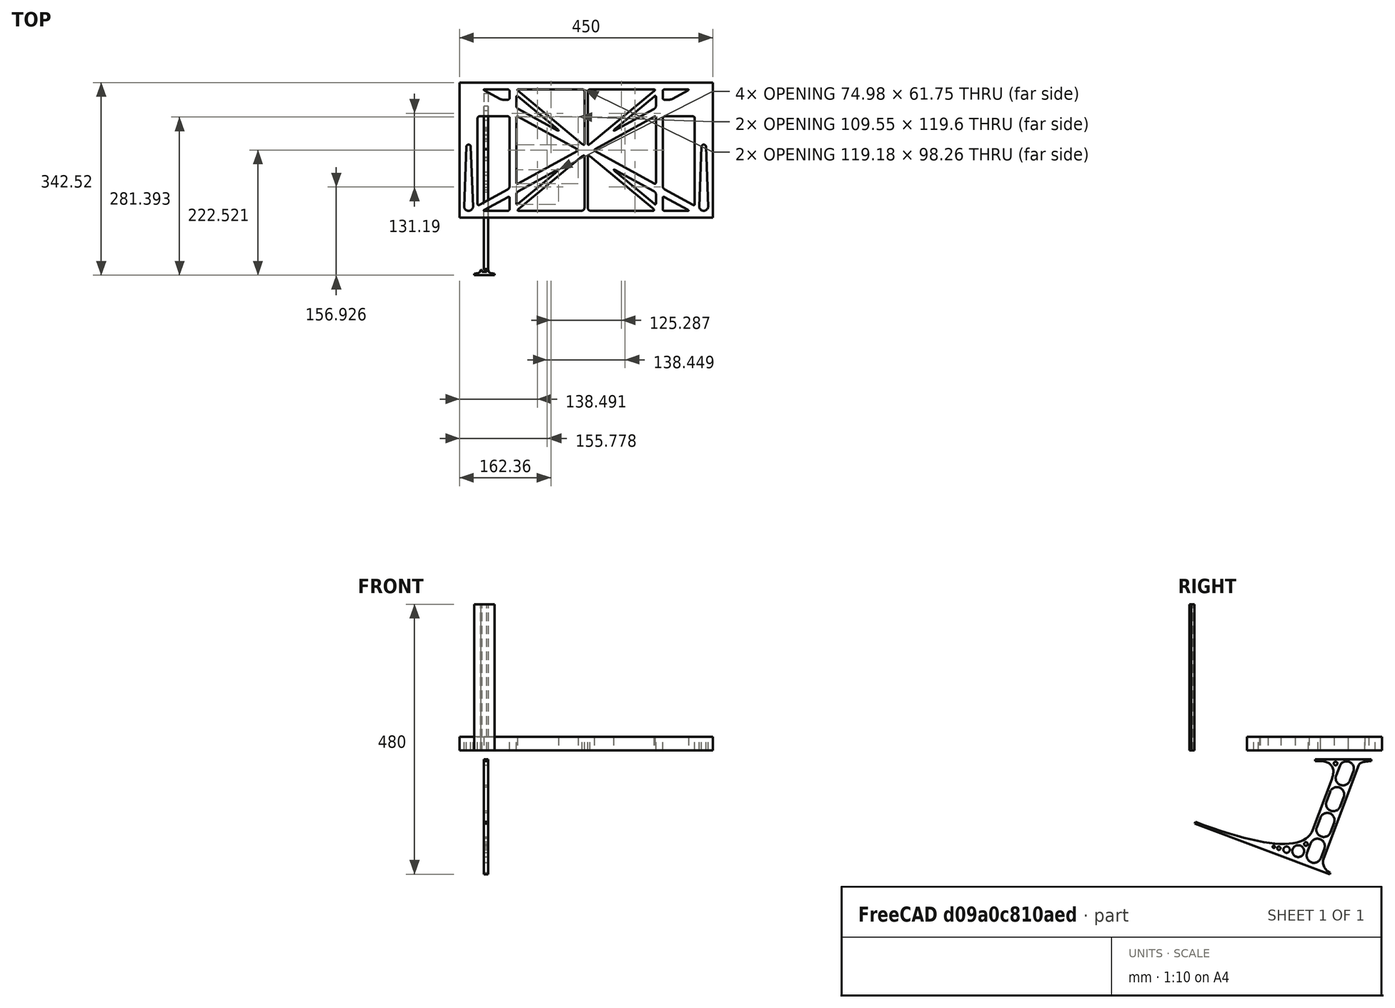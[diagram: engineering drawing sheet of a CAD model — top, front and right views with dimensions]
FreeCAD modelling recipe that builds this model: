
FCSTD DOCUMENT  (FreeCAD 0.19R0.19.2)
Label: laptopStand171FCStd
License: All rights reserved
LicenseURL: http://en.wikipedia.org/wiki/All_rights_reserved
objects: Sketcher::SketchObject×4, Part::Extrusion×3
note: 7 computed .brp shape members not serialized (recipe doc carries the construction recipe); baked Part::Feature solids carry a one-line shape summary decoded from their .brp

FEATURE [Sketcher::SketchObject] Sketch
  FullyConstrained = false
  sketch-geometry (349):
    g0: LineSegment StartX=-10.9272 StartY=-82.7794 StartZ=0 EndX=46.0728 EndY=-51.4823 EndZ=0
    g1: LineSegment StartX=-10.9272 StartY=76.4095 StartZ=0 EndX=-10.9272 EndY=-82.7794 EndZ=0
    g2: LineSegment StartX=46.0728 StartY=76.4095 StartZ=0 EndX=46.0728 EndY=-51.4823 EndZ=0
    g3: LineSegment StartX=-42.9272 StartY=136.221 StartZ=0 EndX=-42.9272 EndY=-103.779 EndZ=0
    g4: LineSegment StartX=407.073 StartY=136.221 StartZ=0 EndX=407.073 EndY=-103.779 EndZ=0
    g5: ArcOfCircle CenterX=-26.9272 CenterY=-83.7794 CenterZ=0 NormalX=0 NormalY=0 NormalZ=1 AngleXU=0 Radius=8 StartAngle=3.14159 EndAngle=6.28319
    g6: ArcOfCircle CenterX=391.073 CenterY=22.1087 CenterZ=0 NormalX=0 NormalY=0 NormalZ=1 AngleXU=0 Radius=8 StartAngle=-4.4e-15 EndAngle=3.14159
    g7: LineSegment StartX=399.073 StartY=22.1087 StartZ=0 EndX=399.073 EndY=-83.7794 EndZ=0
    g8: LineSegment StartX=383.073 StartY=22.1087 StartZ=0 EndX=383.073 EndY=-83.7794 EndZ=0
    g9: ArcOfCircle CenterX=391.073 CenterY=-83.7794 CenterZ=0 NormalX=0 NormalY=0 NormalZ=1 AngleXU=0 Radius=8 StartAngle=3.14159 EndAngle=6.28319
    g10: Circle CenterX=175.022 CenterY=27.0628 CenterZ=0 NormalX=0 NormalY=0 NormalZ=1 AngleXU=0 Radius=1
    g11: Circle CenterX=179.022 CenterY=24.8665 CenterZ=0 NormalX=0 NormalY=0 NormalZ=1 AngleXU=0 Radius=1
    g12: Circle CenterX=179.022 CenterY=27.0628 CenterZ=0 NormalX=0 NormalY=0 NormalZ=1 AngleXU=0 Radius=1
    g13: BSplineCurve PolesCount=3 KnotsCount=2 Degree=2 IsPeriodic=0
    g14: GeomPoint X=175.022 Y=27.0628 Z=0
    g15: GeomPoint X=179.022 Y=27.0628 Z=0
    g16: Circle CenterX=189.124 CenterY=27.0628 CenterZ=0 NormalX=0 NormalY=0 NormalZ=1 AngleXU=0 Radius=1
    g17: Circle CenterX=185.124 CenterY=24.8665 CenterZ=0 NormalX=0 NormalY=0 NormalZ=1 AngleXU=0 Radius=1
    g18: Circle CenterX=185.124 CenterY=27.0628 CenterZ=0 NormalX=0 NormalY=0 NormalZ=1 AngleXU=0 Radius=1
    g19: BSplineCurve PolesCount=3 KnotsCount=2 Degree=2 IsPeriodic=0
    g20: GeomPoint X=189.124 Y=27.0628 Z=0
    g21: GeomPoint X=185.124 Y=27.0628 Z=0
    g22: Circle CenterX=175.022 CenterY=5.37834 CenterZ=0 NormalX=0 NormalY=0 NormalZ=1 AngleXU=0 Radius=1
    g23: Circle CenterX=179.022 CenterY=7.57463 CenterZ=0 NormalX=0 NormalY=0 NormalZ=1 AngleXU=0 Radius=1
    g24: Circle CenterX=179.022 CenterY=5.34704 CenterZ=0 NormalX=0 NormalY=0 NormalZ=1 AngleXU=0 Radius=1
    g25: BSplineCurve PolesCount=3 KnotsCount=2 Degree=2 IsPeriodic=0
    g26: GeomPoint X=175.022 Y=5.37834 Z=0
    g27: GeomPoint X=179.022 Y=5.34704 Z=0
    g28: Circle CenterX=189.124 CenterY=5.37834 CenterZ=0 NormalX=0 NormalY=0 NormalZ=1 AngleXU=0 Radius=1
    g29: Circle CenterX=185.124 CenterY=7.57463 CenterZ=0 NormalX=0 NormalY=0 NormalZ=1 AngleXU=0 Radius=1
    g30: Circle CenterX=185.124 CenterY=5.34704 CenterZ=0 NormalX=0 NormalY=0 NormalZ=1 AngleXU=0 Radius=1
    g31: BSplineCurve PolesCount=3 KnotsCount=2 Degree=2 IsPeriodic=0
    g32: GeomPoint X=189.124 Y=5.37834 Z=0
    g33: GeomPoint X=185.124 Y=5.34704 Z=0
    g34: Circle CenterX=165.871 CenterY=18.1458 CenterZ=0 NormalX=0 NormalY=0 NormalZ=1 AngleXU=0 Radius=1
    g35: Circle CenterX=169.377 CenterY=16.2206 CenterZ=0 NormalX=0 NormalY=0 NormalZ=1 AngleXU=0 Radius=1
    g36: Circle CenterX=165.871 CenterY=14.2954 CenterZ=0 NormalX=0 NormalY=0 NormalZ=1 AngleXU=0 Radius=1
    g37: BSplineCurve PolesCount=3 KnotsCount=2 Degree=2 IsPeriodic=0
    g38: GeomPoint X=165.871 Y=18.1458 Z=0
    g39: GeomPoint X=165.871 Y=14.2954 Z=0
    g40: Circle CenterX=198.275 CenterY=18.1458 CenterZ=0 NormalX=0 NormalY=0 NormalZ=1 AngleXU=0 Radius=1
    g41: Circle CenterX=194.768 CenterY=16.2206 CenterZ=0 NormalX=0 NormalY=0 NormalZ=1 AngleXU=0 Radius=1
    g42: Circle CenterX=198.275 CenterY=14.2954 CenterZ=0 NormalX=0 NormalY=0 NormalZ=1 AngleXU=0 Radius=1
    g43: BSplineCurve PolesCount=3 KnotsCount=2 Degree=2 IsPeriodic=0
    g44: GeomPoint X=198.275 Y=18.1458 Z=0
    g45: GeomPoint X=198.275 Y=14.2954 Z=0
    g46: LineSegment StartX=407.073 StartY=-103.779 StartZ=0 EndX=-42.9272 EndY=-103.779 EndZ=0
    g47: LineSegment StartX=407.073 StartY=136.221 StartZ=0 EndX=-42.9272 EndY=136.221 EndZ=0
    g48: LineSegment StartX=46.0728 StartY=76.4095 StartZ=0 EndX=-10.9272 EndY=76.4095 EndZ=0
    g49: Circle CenterX=125.607 CenterY=54.1951 CenterZ=0 NormalX=0 NormalY=0 NormalZ=1 AngleXU=0 Radius=1
    g50: Circle CenterX=139.632 CenterY=46.4944 CenterZ=0 NormalX=0 NormalY=0 NormalZ=1 AngleXU=0 Radius=1
    g51: Circle CenterX=127.326 CenterY=56.7187 CenterZ=0 NormalX=0 NormalY=0 NormalZ=1 AngleXU=0 Radius=1
    g52: BSplineCurve PolesCount=3 KnotsCount=2 Degree=2 IsPeriodic=0
    g53: GeomPoint X=125.607 Y=54.1951 Z=0
    g54: GeomPoint X=127.326 Y=56.7187 Z=0
    g55: Circle CenterX=236.821 CenterY=56.7187 CenterZ=0 NormalX=0 NormalY=0 NormalZ=1 AngleXU=0 Radius=1
    g56: Circle CenterX=224.513 CenterY=46.4944 CenterZ=0 NormalX=0 NormalY=0 NormalZ=1 AngleXU=0 Radius=1
    g57: Circle CenterX=238.538 CenterY=54.1951 CenterZ=0 NormalX=0 NormalY=0 NormalZ=1 AngleXU=0 Radius=1
    g58: BSplineCurve PolesCount=3 KnotsCount=2 Degree=2 IsPeriodic=0
    g59: GeomPoint X=236.821 Y=56.7187 Z=0
    g60: GeomPoint X=238.538 Y=54.1951 Z=0
    g61: Circle CenterX=238.538 CenterY=-21.7539 CenterZ=0 NormalX=0 NormalY=0 NormalZ=1 AngleXU=0 Radius=1
    g62: Circle CenterX=224.513 CenterY=-14.0532 CenterZ=0 NormalX=0 NormalY=0 NormalZ=1 AngleXU=0 Radius=1
    g63: Circle CenterX=236.821 CenterY=-24.2775 CenterZ=0 NormalX=0 NormalY=0 NormalZ=1 AngleXU=0 Radius=1
    g64: BSplineCurve PolesCount=3 KnotsCount=2 Degree=2 IsPeriodic=0
    g65: GeomPoint X=238.538 Y=-21.7539 Z=0
    g66: GeomPoint X=236.821 Y=-24.2775 Z=0
    g67: Circle CenterX=125.607 CenterY=-21.7539 CenterZ=0 NormalX=0 NormalY=0 NormalZ=1 AngleXU=0 Radius=1
    g68: Circle CenterX=139.632 CenterY=-14.0532 CenterZ=0 NormalX=0 NormalY=0 NormalZ=1 AngleXU=0 Radius=1
    g69: Circle CenterX=127.325 CenterY=-24.2775 CenterZ=0 NormalX=0 NormalY=0 NormalZ=1 AngleXU=0 Radius=1
    g70: BSplineCurve PolesCount=3 KnotsCount=2 Degree=2 IsPeriodic=0
    g71: GeomPoint X=125.607 Y=-21.7539 Z=0
    g72: GeomPoint X=127.325 Y=-24.2775 Z=0
    g73: Circle CenterX=302.996 CenterY=111.695 CenterZ=0 NormalX=0 NormalY=0 NormalZ=1 AngleXU=0 Radius=1
    g74: Circle CenterX=306.073 CenterY=114.251 CenterZ=0 NormalX=0 NormalY=0 NormalZ=1 AngleXU=0 Radius=1
    g75: Circle CenterX=306.073 CenterY=110.251 CenterZ=0 NormalX=0 NormalY=0 NormalZ=1 AngleXU=0 Radius=1
    g76: BSplineCurve PolesCount=3 KnotsCount=2 Degree=2 IsPeriodic=0
    g77: GeomPoint X=302.996 Y=111.695 Z=0
    g78: GeomPoint X=306.073 Y=110.251 Z=0
    g79: Circle CenterX=306.073 CenterY=95.2763 CenterZ=0 NormalX=0 NormalY=0 NormalZ=1 AngleXU=0 Radius=1
    g80: Circle CenterX=306.073 CenterY=91.2763 CenterZ=0 NormalX=0 NormalY=0 NormalZ=1 AngleXU=0 Radius=1
    g81: Circle CenterX=302.567 CenterY=89.3511 CenterZ=0 NormalX=0 NormalY=0 NormalZ=1 AngleXU=0 Radius=1
    g82: BSplineCurve PolesCount=3 KnotsCount=2 Degree=2 IsPeriodic=0
    g83: GeomPoint X=306.073 Y=95.2763 Z=0
    g84: GeomPoint X=302.567 Y=89.3511 Z=0
    g85: LineSegment StartX=306.073 StartY=110.251 StartZ=0 EndX=306.073 EndY=95.2763 EndZ=0
    g86: LineSegment StartX=302.996 StartY=111.695 StartZ=0 EndX=236.821 EndY=56.7187 EndZ=0
    g87: LineSegment StartX=238.538 StartY=54.1951 StartZ=0 EndX=302.567 EndY=89.3511 EndZ=0
    g88: Circle CenterX=61.1496 CenterY=111.695 CenterZ=0 NormalX=0 NormalY=0 NormalZ=1 AngleXU=0 Radius=1
    g89: Circle CenterX=58.0728 CenterY=114.251 CenterZ=0 NormalX=0 NormalY=0 NormalZ=1 AngleXU=0 Radius=1
    g90: Circle CenterX=58.0728 CenterY=110.251 CenterZ=0 NormalX=0 NormalY=0 NormalZ=1 AngleXU=0 Radius=1
    g91: BSplineCurve PolesCount=3 KnotsCount=2 Degree=2 IsPeriodic=0
    g92: GeomPoint X=61.1496 Y=111.695 Z=0
    g93: GeomPoint X=58.0728 Y=110.251 Z=0
    g94: Circle CenterX=61.5791 CenterY=89.3511 CenterZ=0 NormalX=0 NormalY=0 NormalZ=1 AngleXU=0 Radius=1
    g95: Circle CenterX=58.0728 CenterY=91.2763 CenterZ=0 NormalX=0 NormalY=0 NormalZ=1 AngleXU=0 Radius=1
    g96: Circle CenterX=58.0728 CenterY=95.2763 CenterZ=0 NormalX=0 NormalY=0 NormalZ=1 AngleXU=0 Radius=1
    g97: BSplineCurve PolesCount=3 KnotsCount=2 Degree=2 IsPeriodic=0
    g98: GeomPoint X=61.5791 Y=89.3511 Z=0
    g99: GeomPoint X=58.0728 Y=95.2763 Z=0
    g100: LineSegment StartX=58.0728 StartY=110.251 StartZ=0 EndX=58.0728 EndY=95.2763 EndZ=0
    g101: LineSegment StartX=61.1496 StartY=111.695 StartZ=0 EndX=127.326 EndY=56.7187 EndZ=0
    g102: LineSegment StartX=125.607 StartY=54.1951 StartZ=0 EndX=61.5791 EndY=89.3511 EndZ=0
    g103: Circle CenterX=61.5791 CenterY=-56.9099 CenterZ=0 NormalX=0 NormalY=0 NormalZ=1 AngleXU=0 Radius=1
    g104: Circle CenterX=58.0728 CenterY=-58.8351 CenterZ=0 NormalX=0 NormalY=0 NormalZ=1 AngleXU=0 Radius=1
    g105: Circle CenterX=58.0728 CenterY=-62.8351 CenterZ=0 NormalX=0 NormalY=0 NormalZ=1 AngleXU=0 Radius=1
    g106: BSplineCurve PolesCount=3 KnotsCount=2 Degree=2 IsPeriodic=0
    g107: GeomPoint X=61.5791 Y=-56.9099 Z=0
    g108: GeomPoint X=58.0728 Y=-62.8351 Z=0
    g109: Circle CenterX=58.0728 CenterY=-77.8102 CenterZ=0 NormalX=0 NormalY=0 NormalZ=1 AngleXU=0 Radius=1
    g110: Circle CenterX=58.0728 CenterY=-81.8102 CenterZ=0 NormalX=0 NormalY=0 NormalZ=1 AngleXU=0 Radius=1
    g111: Circle CenterX=61.1496 CenterY=-79.2541 CenterZ=0 NormalX=0 NormalY=0 NormalZ=1 AngleXU=0 Radius=1
    g112: BSplineCurve PolesCount=3 KnotsCount=2 Degree=2 IsPeriodic=0
    g113: GeomPoint X=58.0728 Y=-77.8102 Z=0
    g114: GeomPoint X=61.1496 Y=-79.2541 Z=0
    g115: LineSegment StartX=58.0728 StartY=-62.8351 StartZ=0 EndX=58.0728 EndY=-77.8102 EndZ=0
    g116: LineSegment StartX=61.1496 StartY=-79.2541 StartZ=0 EndX=127.325 EndY=-24.2775 EndZ=0
    g117: LineSegment StartX=125.607 StartY=-21.7539 StartZ=0 EndX=61.5791 EndY=-56.9099 EndZ=0
    g118: Circle CenterX=302.567 CenterY=-56.9099 CenterZ=0 NormalX=0 NormalY=0 NormalZ=1 AngleXU=0 Radius=1
    g119: Circle CenterX=306.073 CenterY=-58.8351 CenterZ=0 NormalX=0 NormalY=0 NormalZ=1 AngleXU=0 Radius=1
    g120: Circle CenterX=306.073 CenterY=-62.8351 CenterZ=0 NormalX=0 NormalY=0 NormalZ=1 AngleXU=0 Radius=1
    g121: BSplineCurve PolesCount=3 KnotsCount=2 Degree=2 IsPeriodic=0
    g122: GeomPoint X=302.567 Y=-56.9099 Z=0
    g123: GeomPoint X=306.073 Y=-62.8351 Z=0
    g124: Circle CenterX=302.996 CenterY=-79.2541 CenterZ=0 NormalX=0 NormalY=0 NormalZ=1 AngleXU=0 Radius=1
    g125: Circle CenterX=306.073 CenterY=-81.8102 CenterZ=0 NormalX=0 NormalY=0 NormalZ=1 AngleXU=0 Radius=1
    g126: Circle CenterX=306.073 CenterY=-77.8102 CenterZ=0 NormalX=0 NormalY=0 NormalZ=1 AngleXU=0 Radius=1
    g127: BSplineCurve PolesCount=3 KnotsCount=2 Degree=2 IsPeriodic=0
    g128: GeomPoint X=302.996 Y=-79.2541 Z=0
    g129: GeomPoint X=306.073 Y=-77.8102 Z=0
    g130: LineSegment StartX=306.073 StartY=-62.8351 StartZ=0 EndX=306.073 EndY=-77.8102 EndZ=0
    g131: LineSegment StartX=302.996 StartY=-79.2541 StartZ=0 EndX=236.821 EndY=-24.2775 EndZ=0
    g132: LineSegment StartX=238.538 StartY=-21.7539 StartZ=0 EndX=302.567 EndY=-56.9099 EndZ=0
    g133: Circle CenterX=61.6457 CenterY=-88.8112 CenterZ=0 NormalX=0 NormalY=0 NormalZ=1 AngleXU=0 Radius=1
    g134: Circle CenterX=58.0728 CenterY=-91.7794 CenterZ=0 NormalX=0 NormalY=0 NormalZ=1 AngleXU=0 Radius=1
    g135: Circle CenterX=63.9135 CenterY=-91.7794 CenterZ=0 NormalX=0 NormalY=0 NormalZ=1 AngleXU=0 Radius=1
    g136: BSplineCurve PolesCount=3 KnotsCount=2 Degree=2 IsPeriodic=0
    g137: GeomPoint X=61.6457 Y=-88.8112 Z=0
    g138: GeomPoint X=63.9135 Y=-91.7794 Z=0
    g139: Circle CenterX=179.022 CenterY=-85.8163 CenterZ=0 NormalX=0 NormalY=0 NormalZ=1 AngleXU=0 Radius=1
    g140: Circle CenterX=179.022 CenterY=-91.7794 CenterZ=0 NormalX=0 NormalY=0 NormalZ=1 AngleXU=0 Radius=1
    g141: Circle CenterX=171.895 CenterY=-91.7794 CenterZ=0 NormalX=0 NormalY=0 NormalZ=1 AngleXU=0 Radius=1
    g142: BSplineCurve PolesCount=3 KnotsCount=2 Degree=2 IsPeriodic=0
    g143: GeomPoint X=179.022 Y=-85.8163 Z=0
    g144: GeomPoint X=171.895 Y=-91.7794 Z=0
    g145: Circle CenterX=185.124 CenterY=-86.2028 CenterZ=0 NormalX=0 NormalY=0 NormalZ=1 AngleXU=0 Radius=1
    g146: Circle CenterX=185.124 CenterY=-91.7794 CenterZ=0 NormalX=0 NormalY=0 NormalZ=1 AngleXU=0 Radius=1
    g147: Circle CenterX=191.747 CenterY=-91.7794 CenterZ=0 NormalX=0 NormalY=0 NormalZ=1 AngleXU=0 Radius=1
    g148: BSplineCurve PolesCount=3 KnotsCount=2 Degree=2 IsPeriodic=0
    g149: GeomPoint X=185.124 Y=-86.2028 Z=0
    g150: GeomPoint X=191.747 Y=-91.7794 Z=0
    g151: Circle CenterX=299.888 CenterY=-86.6413 CenterZ=0 NormalX=0 NormalY=0 NormalZ=1 AngleXU=0 Radius=1
    g152: Circle CenterX=306.073 CenterY=-91.7794 CenterZ=0 NormalX=0 NormalY=0 NormalZ=1 AngleXU=0 Radius=1
    g153: Circle CenterX=298.776 CenterY=-91.7794 CenterZ=0 NormalX=0 NormalY=0 NormalZ=1 AngleXU=0 Radius=1
    g154: BSplineCurve PolesCount=3 KnotsCount=2 Degree=2 IsPeriodic=0
    g155: GeomPoint X=299.888 Y=-86.6413 Z=0
    g156: GeomPoint X=298.776 Y=-91.7794 Z=0
    g157: LineSegment StartX=189.124 StartY=5.37834 StartZ=0 EndX=299.888 EndY=-86.6413 EndZ=0
    g158: LineSegment StartX=298.776 StartY=-91.7794 StartZ=0 EndX=191.747 EndY=-91.7794 EndZ=0
    g159: LineSegment StartX=185.124 StartY=-86.2028 StartZ=0 EndX=185.124 EndY=5.34704 EndZ=0
    g160: LineSegment StartX=179.022 StartY=5.34704 StartZ=0 EndX=179.022 EndY=-85.8163 EndZ=0
    g161: LineSegment StartX=171.895 StartY=-91.7794 StartZ=0 EndX=63.9135 EndY=-91.7794 EndZ=0
    g162: LineSegment StartX=61.6457 StartY=-88.8112 StartZ=0 EndX=175.022 EndY=5.37834 EndZ=0
    g163: Circle CenterX=302.073 CenterY=124.221 CenterZ=0 NormalX=0 NormalY=0 NormalZ=1 AngleXU=0 Radius=1
    g164: Circle CenterX=306.073 CenterY=124.221 CenterZ=0 NormalX=0 NormalY=0 NormalZ=1 AngleXU=0 Radius=1
    g165: Circle CenterX=302.996 CenterY=121.665 CenterZ=0 NormalX=0 NormalY=0 NormalZ=1 AngleXU=0 Radius=1
    g166: BSplineCurve PolesCount=3 KnotsCount=2 Degree=2 IsPeriodic=0
    g167: GeomPoint X=302.073 Y=124.221 Z=0
    g168: GeomPoint X=302.996 Y=121.665 Z=0
    g169: Circle CenterX=189.124 CenterY=124.221 CenterZ=0 NormalX=0 NormalY=0 NormalZ=1 AngleXU=0 Radius=1
    g170: Circle CenterX=185.124 CenterY=124.221 CenterZ=0 NormalX=0 NormalY=0 NormalZ=1 AngleXU=0 Radius=1
    g171: Circle CenterX=185.124 CenterY=120.221 CenterZ=0 NormalX=0 NormalY=0 NormalZ=1 AngleXU=0 Radius=1
    g172: BSplineCurve PolesCount=3 KnotsCount=2 Degree=2 IsPeriodic=0
    g173: GeomPoint X=189.124 Y=124.221 Z=0
    g174: GeomPoint X=185.124 Y=120.221 Z=0
    g175: Circle CenterX=175.022 CenterY=124.221 CenterZ=0 NormalX=0 NormalY=0 NormalZ=1 AngleXU=0 Radius=1
    g176: Circle CenterX=179.022 CenterY=124.221 CenterZ=0 NormalX=0 NormalY=0 NormalZ=1 AngleXU=0 Radius=1
    g177: Circle CenterX=179.022 CenterY=120.221 CenterZ=0 NormalX=0 NormalY=0 NormalZ=1 AngleXU=0 Radius=1
    g178: BSplineCurve PolesCount=3 KnotsCount=2 Degree=2 IsPeriodic=0
    g179: GeomPoint X=175.022 Y=124.221 Z=0
    g180: GeomPoint X=179.022 Y=120.221 Z=0
    g181: Circle CenterX=62.0728 CenterY=124.221 CenterZ=0 NormalX=0 NormalY=0 NormalZ=1 AngleXU=0 Radius=1
    g182: Circle CenterX=58.0728 CenterY=124.221 CenterZ=0 NormalX=0 NormalY=0 NormalZ=1 AngleXU=0 Radius=1
    g183: Circle CenterX=61.1496 CenterY=121.665 CenterZ=0 NormalX=0 NormalY=0 NormalZ=1 AngleXU=0 Radius=1
    g184: BSplineCurve PolesCount=3 KnotsCount=2 Degree=2 IsPeriodic=0
    g185: GeomPoint X=62.0728 Y=124.221 Z=0
    g186: GeomPoint X=61.1496 Y=121.665 Z=0
    g187: LineSegment StartX=62.0728 StartY=124.221 StartZ=0 EndX=175.022 EndY=124.221 EndZ=0
    g188: LineSegment StartX=179.022 StartY=120.221 StartZ=0 EndX=179.022 EndY=27.0628 EndZ=0
    g189: LineSegment StartX=185.124 StartY=27.0628 StartZ=0 EndX=185.124 EndY=120.221 EndZ=0
    g190: LineSegment StartX=189.124 StartY=124.221 StartZ=0 EndX=302.073 EndY=124.221 EndZ=0
    g191: LineSegment StartX=302.996 StartY=121.665 StartZ=0 EndX=189.124 EndY=27.0628 EndZ=0
    g192: LineSegment StartX=175.022 StartY=27.0628 StartZ=0 EndX=61.1496 EndY=121.665 EndZ=0
    g193: Circle CenterX=61.5791 CenterY=75.4095 CenterZ=0 NormalX=0 NormalY=0 NormalZ=1 AngleXU=0 Radius=1
    g194: Circle CenterX=58.0728 CenterY=77.3346 CenterZ=0 NormalX=0 NormalY=0 NormalZ=1 AngleXU=0 Radius=1
    g195: Circle CenterX=58.0728 CenterY=73.3346 CenterZ=0 NormalX=0 NormalY=0 NormalZ=1 AngleXU=0 Radius=1
    g196: BSplineCurve PolesCount=3 KnotsCount=2 Degree=2 IsPeriodic=0
    g197: GeomPoint X=61.5791 Y=75.4095 Z=0
    g198: GeomPoint X=58.0728 Y=73.3346 Z=0
    g199: Circle CenterX=58.0728 CenterY=-40.8935 CenterZ=0 NormalX=0 NormalY=0 NormalZ=1 AngleXU=0 Radius=1
    g200: Circle CenterX=58.0728 CenterY=-44.8935 CenterZ=0 NormalX=0 NormalY=0 NormalZ=1 AngleXU=0 Radius=1
    g201: Circle CenterX=61.5791 CenterY=-42.9683 CenterZ=0 NormalX=0 NormalY=0 NormalZ=1 AngleXU=0 Radius=1
    g202: BSplineCurve PolesCount=3 KnotsCount=2 Degree=2 IsPeriodic=0
    g203: GeomPoint X=58.0728 Y=-40.8935 Z=0
    g204: GeomPoint X=61.5791 Y=-42.9683 Z=0
    g205: LineSegment StartX=61.5791 StartY=-42.9683 StartZ=0 EndX=165.871 EndY=14.2954 EndZ=0
    g206: LineSegment StartX=165.871 StartY=18.1458 StartZ=0 EndX=61.5791 EndY=75.4095 EndZ=0
    g207: LineSegment StartX=58.0728 StartY=73.3346 StartZ=0 EndX=58.0728 EndY=-40.8935 EndZ=0
    g208: Circle CenterX=302.567 CenterY=-42.9683 CenterZ=0 NormalX=0 NormalY=0 NormalZ=1 AngleXU=0 Radius=1
    g209: Circle CenterX=306.073 CenterY=-44.8935 CenterZ=0 NormalX=0 NormalY=0 NormalZ=1 AngleXU=0 Radius=1
    g210: Circle CenterX=306.073 CenterY=-40.8935 CenterZ=0 NormalX=0 NormalY=0 NormalZ=1 AngleXU=0 Radius=1
    g211: BSplineCurve PolesCount=3 KnotsCount=2 Degree=2 IsPeriodic=0
    g212: GeomPoint X=302.567 Y=-42.9683 Z=0
    g213: GeomPoint X=306.073 Y=-40.8935 Z=0
    g214: Circle CenterX=306.073 CenterY=73.3346 CenterZ=0 NormalX=0 NormalY=0 NormalZ=1 AngleXU=0 Radius=1
    g215: Circle CenterX=306.073 CenterY=77.3346 CenterZ=0 NormalX=0 NormalY=0 NormalZ=1 AngleXU=0 Radius=1
    g216: Circle CenterX=302.567 CenterY=75.4095 CenterZ=0 NormalX=0 NormalY=0 NormalZ=1 AngleXU=0 Radius=1
    g217: BSplineCurve PolesCount=3 KnotsCount=2 Degree=2 IsPeriodic=0
    g218: GeomPoint X=306.073 Y=73.3346 Z=0
    g219: GeomPoint X=302.567 Y=75.4095 Z=0
    g220: LineSegment StartX=302.567 StartY=-42.9683 StartZ=0 EndX=198.275 EndY=14.2954 EndZ=0
    g221: LineSegment StartX=198.275 StartY=18.1458 StartZ=0 EndX=302.567 EndY=75.4095 EndZ=0
    g222: LineSegment StartX=306.073 StartY=73.3346 StartZ=0 EndX=306.073 EndY=-40.8935 EndZ=0
    g223: LineSegment StartX=322.073 StartY=105.865 StartZ=0 EndX=328.643 EndY=105.865 EndZ=0
    g224: LineSegment StartX=318.073 StartY=120.221 StartZ=0 EndX=318.073 EndY=109.865 EndZ=0
    g225: LineSegment StartX=336.157 StartY=107.779 StartZ=0 EndX=362.567 EndY=122.294 EndZ=0
    g226: Circle CenterX=362.073 CenterY=124.221 CenterZ=0 NormalX=0 NormalY=0 NormalZ=1 AngleXU=0 Radius=1
    g227: Circle CenterX=366.073 CenterY=124.221 CenterZ=0 NormalX=0 NormalY=0 NormalZ=1 AngleXU=0 Radius=1
    g228: Circle CenterX=362.567 CenterY=122.294 CenterZ=0 NormalX=0 NormalY=0 NormalZ=1 AngleXU=0 Radius=1
    g229: BSplineCurve PolesCount=3 KnotsCount=2 Degree=2 IsPeriodic=0
    g230: GeomPoint X=362.073 Y=124.221 Z=0
    g231: GeomPoint X=362.567 Y=122.294 Z=0
    g232: Circle CenterX=322.073 CenterY=124.221 CenterZ=0 NormalX=0 NormalY=0 NormalZ=1 AngleXU=0 Radius=1
    g233: Circle CenterX=318.073 CenterY=124.221 CenterZ=0 NormalX=0 NormalY=0 NormalZ=1 AngleXU=0 Radius=1
    g234: Circle CenterX=318.073 CenterY=120.221 CenterZ=0 NormalX=0 NormalY=0 NormalZ=1 AngleXU=0 Radius=1
    g235: BSplineCurve PolesCount=3 KnotsCount=2 Degree=2 IsPeriodic=0
    g236: GeomPoint X=322.073 Y=124.221 Z=0
    g237: GeomPoint X=318.073 Y=120.221 Z=0
    g238: Circle CenterX=322.073 CenterY=105.865 CenterZ=0 NormalX=0 NormalY=0 NormalZ=1 AngleXU=0 Radius=1
    g239: Circle CenterX=318.073 CenterY=105.865 CenterZ=0 NormalX=0 NormalY=0 NormalZ=1 AngleXU=0 Radius=1
    g240: Circle CenterX=318.073 CenterY=109.865 CenterZ=0 NormalX=0 NormalY=0 NormalZ=1 AngleXU=0 Radius=1
    g241: BSplineCurve PolesCount=3 KnotsCount=2 Degree=2 IsPeriodic=0
    g242: GeomPoint X=322.073 Y=105.865 Z=0
    g243: GeomPoint X=318.073 Y=109.865 Z=0
    g244: Circle CenterX=336.157 CenterY=107.779 CenterZ=0 NormalX=0 NormalY=0 NormalZ=1 AngleXU=0 Radius=1
    g245: Circle CenterX=332.651 CenterY=105.853 CenterZ=0 NormalX=0 NormalY=0 NormalZ=1 AngleXU=0 Radius=1
    g246: Circle CenterX=328.643 CenterY=105.865 CenterZ=0 NormalX=0 NormalY=0 NormalZ=1 AngleXU=0 Radius=1
    g247: BSplineCurve PolesCount=3 KnotsCount=2 Degree=2 IsPeriodic=0
    g248: GeomPoint X=336.157 Y=107.779 Z=0
    g249: GeomPoint X=328.643 Y=105.865 Z=0
    g250: LineSegment StartX=322.073 StartY=124.221 StartZ=0 EndX=362.073 EndY=124.221 EndZ=0
    g251: Circle CenterX=371.567 CenterY=-80.8644 CenterZ=0 NormalX=0 NormalY=0 NormalZ=1 AngleXU=0 Radius=1
    g252: Circle CenterX=375.073 CenterY=-82.7896 CenterZ=0 NormalX=0 NormalY=0 NormalZ=1 AngleXU=0 Radius=1
    g253: Circle CenterX=375.073 CenterY=-78.7896 CenterZ=0 NormalX=0 NormalY=0 NormalZ=1 AngleXU=0 Radius=1
    g254: BSplineCurve PolesCount=3 KnotsCount=2 Degree=2 IsPeriodic=0
    g255: GeomPoint X=371.567 Y=-80.8644 Z=0
    g256: GeomPoint X=375.073 Y=-78.7896 Z=0
    g257: Circle CenterX=321.579 CenterY=-53.4075 CenterZ=0 NormalX=0 NormalY=0 NormalZ=1 AngleXU=0 Radius=1
    g258: Circle CenterX=318.073 CenterY=-51.4823 CenterZ=0 NormalX=0 NormalY=0 NormalZ=1 AngleXU=0 Radius=1
    g259: Circle CenterX=318.073 CenterY=-47.4805 CenterZ=0 NormalX=0 NormalY=0 NormalZ=1 AngleXU=0 Radius=1
    g260: BSplineCurve PolesCount=3 KnotsCount=2 Degree=2 IsPeriodic=0
    g261: GeomPoint X=321.579 Y=-53.4075 Z=0
    g262: GeomPoint X=318.073 Y=-47.4805 Z=0
    g263: LineSegment StartX=371.567 StartY=-80.8644 StartZ=0 EndX=321.579 EndY=-53.4075 EndZ=0
    g264: Circle CenterX=321.579 CenterY=-67.3492 CenterZ=0 NormalX=0 NormalY=0 NormalZ=1 AngleXU=0 Radius=1
    g265: Circle CenterX=318.073 CenterY=-65.424 CenterZ=0 NormalX=0 NormalY=0 NormalZ=1 AngleXU=0 Radius=1
    g266: Circle CenterX=318.073 CenterY=-69.424 CenterZ=0 NormalX=0 NormalY=0 NormalZ=1 AngleXU=0 Radius=1
    g267: BSplineCurve PolesCount=3 KnotsCount=2 Degree=2 IsPeriodic=0
    g268: GeomPoint X=321.579 Y=-67.3492 Z=0
    g269: GeomPoint X=318.073 Y=-69.424 Z=0
    g270: Circle CenterX=362.567 CenterY=-89.8542 CenterZ=0 NormalX=0 NormalY=0 NormalZ=1 AngleXU=0 Radius=1
    g271: Circle CenterX=366.073 CenterY=-91.7794 CenterZ=0 NormalX=0 NormalY=0 NormalZ=1 AngleXU=0 Radius=1
    g272: Circle CenterX=362.073 CenterY=-91.7794 CenterZ=0 NormalX=0 NormalY=0 NormalZ=1 AngleXU=0 Radius=1
    g273: BSplineCurve PolesCount=3 KnotsCount=2 Degree=2 IsPeriodic=0
    g274: GeomPoint X=362.567 Y=-89.8542 Z=0
    g275: GeomPoint X=362.073 Y=-91.7794 Z=0
    g276: Circle CenterX=322.073 CenterY=-91.7794 CenterZ=0 NormalX=0 NormalY=0 NormalZ=1 AngleXU=0 Radius=1
    g277: Circle CenterX=318.073 CenterY=-91.7794 CenterZ=0 NormalX=0 NormalY=0 NormalZ=1 AngleXU=0 Radius=1
    g278: Circle CenterX=318.073 CenterY=-87.7794 CenterZ=0 NormalX=0 NormalY=0 NormalZ=1 AngleXU=0 Radius=1
    g279: BSplineCurve PolesCount=3 KnotsCount=2 Degree=2 IsPeriodic=0
    g280: GeomPoint X=322.073 Y=-91.7794 Z=0
    g281: GeomPoint X=318.073 Y=-87.7794 Z=0
    g282: LineSegment StartX=362.567 StartY=-89.8542 StartZ=0 EndX=321.579 EndY=-67.3492 EndZ=0
    g283: LineSegment StartX=318.073 StartY=-69.424 StartZ=0 EndX=318.073 EndY=-87.7794 EndZ=0
    g284: LineSegment StartX=322.073 StartY=-91.7794 StartZ=0 EndX=362.073 EndY=-91.7794 EndZ=0
    g285: Circle CenterX=2.07281 CenterY=124.221 CenterZ=0 NormalX=0 NormalY=0 NormalZ=1 AngleXU=0 Radius=1
    g286: Circle CenterX=1.57905 CenterY=122.295 CenterZ=0 NormalX=0 NormalY=0 NormalZ=1 AngleXU=0 Radius=1
    g287: BSplineCurve PolesCount=3 KnotsCount=2 Degree=2 IsPeriodic=0
    g288: GeomPoint X=2.07281 Y=124.221 Z=0
    g289: GeomPoint X=1.57905 Y=122.295 Z=0
    g290: Circle CenterX=42.0728 CenterY=124.221 CenterZ=0 NormalX=0 NormalY=0 NormalZ=1 AngleXU=0 Radius=1
    g291: Circle CenterX=46.0728 CenterY=124.221 CenterZ=0 NormalX=0 NormalY=0 NormalZ=1 AngleXU=0 Radius=1
    g292: Circle CenterX=46.0728 CenterY=120.221 CenterZ=0 NormalX=0 NormalY=0 NormalZ=1 AngleXU=0 Radius=1
    g293: BSplineCurve PolesCount=3 KnotsCount=2 Degree=2 IsPeriodic=0
    g294: GeomPoint X=42.0728 Y=124.221 Z=0
    g295: GeomPoint X=46.0728 Y=120.221 Z=0
    g296: Circle CenterX=46.0728 CenterY=109.865 CenterZ=0 NormalX=0 NormalY=0 NormalZ=1 AngleXU=0 Radius=1
    g297: Circle CenterX=46.0728 CenterY=105.865 CenterZ=0 NormalX=0 NormalY=0 NormalZ=1 AngleXU=0 Radius=1
    g298: Circle CenterX=42.0728 CenterY=105.865 CenterZ=0 NormalX=0 NormalY=0 NormalZ=1 AngleXU=0 Radius=1
    g299: BSplineCurve PolesCount=3 KnotsCount=2 Degree=2 IsPeriodic=0
    g300: GeomPoint X=46.0728 Y=109.865 Z=0
    g301: GeomPoint X=42.0728 Y=105.865 Z=0
    g302: Circle CenterX=35.5028 CenterY=105.865 CenterZ=0 NormalX=0 NormalY=0 NormalZ=1 AngleXU=0 Radius=1
    g303: Circle CenterX=31.5028 CenterY=105.865 CenterZ=0 NormalX=0 NormalY=0 NormalZ=1 AngleXU=0 Radius=1
    g304: Circle CenterX=27.9965 CenterY=107.79 CenterZ=0 NormalX=0 NormalY=0 NormalZ=1 AngleXU=0 Radius=1
    g305: BSplineCurve PolesCount=3 KnotsCount=2 Degree=2 IsPeriodic=0
    g306: GeomPoint X=35.5028 Y=105.865 Z=0
    g307: GeomPoint X=27.9965 Y=107.79 Z=0
    g308: LineSegment StartX=2.07281 StartY=124.221 StartZ=0 EndX=42.0728 EndY=124.221 EndZ=0
    g309: LineSegment StartX=46.0728 StartY=120.221 StartZ=0 EndX=46.0728 EndY=109.865 EndZ=0
    g310: LineSegment StartX=42.0728 StartY=105.865 StartZ=0 EndX=35.5028 EndY=105.865 EndZ=0
    g311: LineSegment StartX=27.9965 StartY=107.79 StartZ=0 EndX=1.57905 EndY=122.295 EndZ=0
    g312: Circle CenterX=42.5666 CenterY=-67.3492 CenterZ=0 NormalX=0 NormalY=0 NormalZ=1 AngleXU=0 Radius=1
    g313: Circle CenterX=46.0728 CenterY=-65.424 CenterZ=0 NormalX=0 NormalY=0 NormalZ=1 AngleXU=0 Radius=1
    g314: Circle CenterX=46.0728 CenterY=-69.424 CenterZ=0 NormalX=0 NormalY=0 NormalZ=1 AngleXU=0 Radius=1
    g315: BSplineCurve PolesCount=3 KnotsCount=2 Degree=2 IsPeriodic=0
    g316: GeomPoint X=42.5666 Y=-67.3492 Z=0
    g317: GeomPoint X=46.0728 Y=-69.424 Z=0
    g318: Circle CenterX=46.0728 CenterY=-87.7794 CenterZ=0 NormalX=0 NormalY=0 NormalZ=1 AngleXU=0 Radius=1
    g319: Circle CenterX=46.0728 CenterY=-91.7794 CenterZ=0 NormalX=0 NormalY=0 NormalZ=1 AngleXU=0 Radius=1
    g320: Circle CenterX=42.0728 CenterY=-91.7794 CenterZ=0 NormalX=0 NormalY=0 NormalZ=1 AngleXU=0 Radius=1
    g321: BSplineCurve PolesCount=3 KnotsCount=2 Degree=2 IsPeriodic=0
    g322: GeomPoint X=46.0728 Y=-87.7794 Z=0
    g323: GeomPoint X=42.0728 Y=-91.7794 Z=0
    g324: Circle CenterX=2.07281 CenterY=-91.7794 CenterZ=0 NormalX=0 NormalY=0 NormalZ=1 AngleXU=0 Radius=1
    g325: Circle CenterX=-1.92719 CenterY=-91.7794 CenterZ=0 NormalX=0 NormalY=0 NormalZ=1 AngleXU=0 Radius=1
    g326: Circle CenterX=1.57905 CenterY=-89.8542 CenterZ=0 NormalX=0 NormalY=0 NormalZ=1 AngleXU=0 Radius=1
    g327: BSplineCurve PolesCount=3 KnotsCount=2 Degree=2 IsPeriodic=0
    g328: GeomPoint X=2.07281 Y=-91.7794 Z=0
    g329: GeomPoint X=1.57905 Y=-89.8542 Z=0
    g330: LineSegment StartX=2.07281 StartY=-91.7794 StartZ=0 EndX=42.0728 EndY=-91.7794 EndZ=0
    g331: LineSegment StartX=46.0728 StartY=-87.7794 StartZ=0 EndX=46.0728 EndY=-69.424 EndZ=0
    g332: LineSegment StartX=42.5666 StartY=-67.3492 StartZ=0 EndX=1.57905 EndY=-89.8542 EndZ=0
    g333: Circle CenterX=322.073 CenterY=76.4095 CenterZ=0 NormalX=0 NormalY=0 NormalZ=1 AngleXU=0 Radius=4
    g334: BSplineCurve PolesCount=3 KnotsCount=2 Degree=2 IsPeriodic=0
    g335: GeomPoint X=318.073 Y=72.4095 Z=0
    g336: GeomPoint X=322.073 Y=76.4095 Z=0
    g337: Circle CenterX=375.073 CenterY=72.4095 CenterZ=0 NormalX=0 NormalY=0 NormalZ=1 AngleXU=0 Radius=1
    g338: Circle CenterX=375.073 CenterY=76.4095 CenterZ=0 NormalX=0 NormalY=0 NormalZ=1 AngleXU=0 Radius=1
    g339: Circle CenterX=371.073 CenterY=76.4095 CenterZ=0 NormalX=0 NormalY=0 NormalZ=1 AngleXU=0 Radius=1
    g340: BSplineCurve PolesCount=3 KnotsCount=2 Degree=2 IsPeriodic=0
    g341: GeomPoint X=375.073 Y=72.4095 Z=0
    g342: GeomPoint X=371.073 Y=76.4095 Z=0
    g343: LineSegment StartX=322.073 StartY=76.4095 StartZ=0 EndX=371.073 EndY=76.4095 EndZ=0
    g344: LineSegment StartX=318.073 StartY=72.4095 StartZ=0 EndX=318.073 EndY=-47.4805 EndZ=0
    g345: LineSegment StartX=375.073 StartY=72.4095 StartZ=0 EndX=375.073 EndY=-78.7896 EndZ=0
    g346: ArcOfCircle CenterX=-26.9272 CenterY=22.1087 CenterZ=0 NormalX=0 NormalY=0 NormalZ=1 AngleXU=0 Radius=4 StartAngle=5e-16 EndAngle=3.14159
    g347: LineSegment StartX=-30.9272 StartY=22.1087 StartZ=0 EndX=-34.9272 EndY=-83.7794 EndZ=0
    g348: LineSegment StartX=-18.9272 StartY=-83.7794 StartZ=0 EndX=-22.9272 EndY=22.1087 EndZ=0
  constraints (572):
    c: Coincident(g0,g2)
    c: Block(g0)
    c: Block(g1)
    c: Vertical(g3)
    c: Vertical(g4)
    c: Block(g4)
    c: Block(g3)
    c: Tangent(g6,g7) = 1.5708
    c: Tangent(g7,g9) = 1.5708
    c: Equal(g6,g9)
    c: Coincident(g8,g6)
    c: Coincident(g8,g9)
    c: Block(g7)
    c: Block(g8)
    c: Weight(g10) = 1
    c: Equal(g10,g11)
    c: Equal(g10,g12)
    c: InternalAlignment(g10,g13)
    c: InternalAlignment(g11,g13)
    c: InternalAlignment(g12,g13)
    c: InternalAlignment(g14,g13)
    c: InternalAlignment(g15,g13)
    c: Weight(g16) = 1
    c: Equal(g16,g17)
    c: Equal(g16,g18)
    c: InternalAlignment(g16,g19)
    c: InternalAlignment(g17,g19)
    c: InternalAlignment(g18,g19)
    c: InternalAlignment(g20,g19)
    c: InternalAlignment(g21,g19)
    c: Block(g19)
    c: Block(g13)
    c: Weight(g22) = 1
    c: Equal(g22,g23)
    c: Equal(g22,g24)
    c: InternalAlignment(g22,g25)
    c: InternalAlignment(g23,g25)
    c: InternalAlignment(g24,g25)
    c: InternalAlignment(g26,g25)
    c: InternalAlignment(g27,g25)
    c: Weight(g28) = 1
    c: Equal(g28,g29)
    c: Equal(g28,g30)
    c: InternalAlignment(g28,g31)
    c: InternalAlignment(g29,g31)
    c: InternalAlignment(g30,g31)
    c: InternalAlignment(g32,g31)
    c: InternalAlignment(g33,g31)
    c: Block(g31)
    c: Block(g25)
    c: Weight(g34) = 1
    c: Equal(g34,g35)
    c: Equal(g34,g36)
    c: InternalAlignment(g34,g37)
    c: InternalAlignment(g35,g37)
    c: InternalAlignment(g36,g37)
    c: InternalAlignment(g38,g37)
    c: InternalAlignment(g39,g37)
    c: Weight(g40) = 1
    c: Equal(g40,g41)
    c: Equal(g40,g42)
    c: InternalAlignment(g40,g43)
    c: InternalAlignment(g41,g43)
    c: InternalAlignment(g42,g43)
    c: InternalAlignment(g44,g43)
    c: InternalAlignment(g45,g43)
    c: Block(g37)
    c: Block(g43)
    c: Coincident(g46,g4)
    c: Coincident(g46,g3)
    c: Horizontal(g46)
    c: Distance(g46) = 450
    c: Coincident(g47,g4)
    c: Coincident(g47,g3)
    c: Horizontal(g47)
    c: Horizontal(g48)
    c: Coincident(g2,g48)
    c: Block(g48)
    c: Coincident(g1,g48)
    c: Weight(g49) = 1
    c: Equal(g49,g50)
    c: Equal(g49,g51)
    c: InternalAlignment(g49,g52)
    c: InternalAlignment(g50,g52)
    c: InternalAlignment(g51,g52)
    c: InternalAlignment(g53,g52)
    c: InternalAlignment(g54,g52)
    c: Block(g52)
    c: Weight(g55) = 1
    c: Equal(g55,g56)
    c: Equal(g55,g57)
    c: InternalAlignment(g55,g58)
    c: InternalAlignment(g56,g58)
    c: InternalAlignment(g57,g58)
    c: InternalAlignment(g59,g58)
    c: InternalAlignment(g60,g58)
    c: Block(g58)
    c: Weight(g61) = 1
    c: Equal(g61,g62)
    c: Equal(g61,g63)
    c: InternalAlignment(g61,g64)
    c: InternalAlignment(g62,g64)
    c: InternalAlignment(g63,g64)
    c: InternalAlignment(g65,g64)
    c: InternalAlignment(g66,g64)
    c: Block(g64)
    c: Weight(g67) = 1
    c: Equal(g67,g68)
    c: Equal(g67,g69)
    c: InternalAlignment(g67,g70)
    c: InternalAlignment(g68,g70)
    c: InternalAlignment(g69,g70)
    c: InternalAlignment(g71,g70)
    c: InternalAlignment(g72,g70)
    c: Block(g70)
    c: Weight(g73) = 1
    c: Equal(g73,g74)
    c: Equal(g73,g75)
    c: InternalAlignment(g73,g76)
    c: InternalAlignment(g74,g76)
    c: InternalAlignment(g75,g76)
    c: InternalAlignment(g77,g76)
    c: InternalAlignment(g78,g76)
    c: Weight(g79) = 1
    c: Equal(g79,g80)
    c: Equal(g79,g81)
    c: InternalAlignment(g79,g82)
    c: InternalAlignment(g80,g82)
    c: InternalAlignment(g81,g82)
    c: InternalAlignment(g83,g82)
    c: InternalAlignment(g84,g82)
    c: Block(g76)
    c: Block(g82)
    c: Coincident(g85,g76)
    c: Coincident(g85,g82)
    c: Vertical(g85)
    c: Coincident(g86,g76)
    c: Coincident(g86,g58)
    c: Coincident(g87,g58)
    c: Coincident(g87,g82)
    c: Weight(g88) = 1
    c: Equal(g88,g89)
    c: Equal(g88,g90)
    c: InternalAlignment(g88,g91)
    c: InternalAlignment(g89,g91)
    c: InternalAlignment(g90,g91)
    c: InternalAlignment(g92,g91)
    c: InternalAlignment(g93,g91)
    c: Weight(g94) = 1
    c: Equal(g94,g95)
    c: Equal(g94,g96)
    c: InternalAlignment(g94,g97)
    c: InternalAlignment(g95,g97)
    c: InternalAlignment(g96,g97)
    c: InternalAlignment(g98,g97)
    c: InternalAlignment(g99,g97)
    c: Block(g91)
    c: Block(g97)
    c: Coincident(g100,g91)
    c: Coincident(g100,g97)
    c: Vertical(g100)
    c: Coincident(g101,g91)
    c: Coincident(g101,g52)
    c: Coincident(g102,g52)
    c: Coincident(g102,g97)
    c: Weight(g103) = 1
    c: Equal(g103,g104)
    c: Equal(g103,g105)
    c: InternalAlignment(g103,g106)
    c: InternalAlignment(g104,g106)
    c: InternalAlignment(g105,g106)
    c: InternalAlignment(g107,g106)
    c: InternalAlignment(g108,g106)
    c: Weight(g109) = 1
    c: Equal(g109,g110)
    c: Equal(g109,g111)
    c: InternalAlignment(g109,g112)
    c: InternalAlignment(g110,g112)
    c: InternalAlignment(g111,g112)
    c: InternalAlignment(g113,g112)
    c: InternalAlignment(g114,g112)
    c: Block(g106)
    c: Block(g112)
    c: Coincident(g115,g106)
    c: Coincident(g115,g112)
    c: Vertical(g115)
    c: Coincident(g116,g112)
    c: Coincident(g116,g70)
    c: Coincident(g117,g70)
    c: Coincident(g117,g106)
    c: Weight(g118) = 1
    c: Equal(g118,g119)
    c: Equal(g118,g120)
    c: InternalAlignment(g118,g121)
    c: InternalAlignment(g119,g121)
    c: InternalAlignment(g120,g121)
    c: InternalAlignment(g122,g121)
    c: InternalAlignment(g123,g121)
    c: Weight(g124) = 1
    c: Equal(g124,g125)
    c: Equal(g124,g126)
    c: InternalAlignment(g124,g127)
    c: InternalAlignment(g125,g127)
    c: InternalAlignment(g126,g127)
    c: InternalAlignment(g128,g127)
    c: InternalAlignment(g129,g127)
    c: Block(g121)
    c: Block(g127)
    c: Coincident(g130,g121)
    c: Coincident(g130,g127)
    c: Vertical(g130)
    c: Coincident(g131,g127)
    c: Coincident(g131,g64)
    c: Coincident(g132,g64)
    c: Coincident(g132,g121)
    c: Weight(g133) = 1
    c: Equal(g133,g134)
    c: Equal(g133,g135)
    c: InternalAlignment(g133,g136)
    c: InternalAlignment(g134,g136)
    c: InternalAlignment(g135,g136)
    c: InternalAlignment(g137,g136)
    c: InternalAlignment(g138,g136)
    c: Weight(g139) = 1
    c: Equal(g139,g140)
    c: Equal(g139,g141)
    c: InternalAlignment(g139,g142)
    c: InternalAlignment(g140,g142)
    c: InternalAlignment(g141,g142)
    c: InternalAlignment(g143,g142)
    c: InternalAlignment(g144,g142)
    c: Weight(g145) = 1
    c: Equal(g145,g146)
    c: Equal(g145,g147)
    c: InternalAlignment(g145,g148)
    c: InternalAlignment(g146,g148)
    c: InternalAlignment(g147,g148)
    c: InternalAlignment(g149,g148)
    c: InternalAlignment(g150,g148)
    c: Weight(g151) = 1
    c: Equal(g151,g152)
    c: Equal(g151,g153)
    c: InternalAlignment(g151,g154)
    c: InternalAlignment(g152,g154)
    c: InternalAlignment(g153,g154)
    c: InternalAlignment(g155,g154)
    c: InternalAlignment(g156,g154)
    c: Block(g154)
    c: Block(g148)
    c: Block(g142)
    c: Block(g136)
    c: Coincident(g157,g31)
    c: Coincident(g157,g154)
    c: Coincident(g158,g154)
    c: Coincident(g158,g148)
    c: Horizontal(g158)
    c: Coincident(g159,g148)
    c: Coincident(g159,g31)
    c: Vertical(g159)
    c: Coincident(g160,g25)
    c: Coincident(g160,g142)
    c: Vertical(g160)
    c: Coincident(g161,g142)
    c: Coincident(g161,g136)
    c: Horizontal(g161)
    c: Coincident(g162,g136)
    c: Coincident(g162,g25)
    c: Weight(g163) = 1
    c: Equal(g163,g164)
    c: Equal(g163,g165)
    c: InternalAlignment(g163,g166)
    c: InternalAlignment(g164,g166)
    c: InternalAlignment(g165,g166)
    c: InternalAlignment(g167,g166)
    c: InternalAlignment(g168,g166)
    c: Weight(g169) = 1
    c: Equal(g169,g170)
    c: Equal(g169,g171)
    c: InternalAlignment(g169,g172)
    c: InternalAlignment(g170,g172)
    c: InternalAlignment(g171,g172)
    c: InternalAlignment(g173,g172)
    c: InternalAlignment(g174,g172)
    c: Weight(g175) = 1
    c: Equal(g175,g176)
    c: Equal(g175,g177)
    c: InternalAlignment(g175,g178)
    c: InternalAlignment(g176,g178)
    c: InternalAlignment(g177,g178)
    c: InternalAlignment(g179,g178)
    c: InternalAlignment(g180,g178)
    c: Weight(g181) = 1
    c: Equal(g181,g182)
    c: Equal(g181,g183)
    c: InternalAlignment(g181,g184)
    c: InternalAlignment(g182,g184)
    c: InternalAlignment(g183,g184)
    c: InternalAlignment(g185,g184)
    c: InternalAlignment(g186,g184)
    c: Block(g184)
    c: Block(g178)
    c: Block(g172)
    c: Block(g166)
    c: Coincident(g187,g184)
    c: Coincident(g187,g178)
    c: Horizontal(g187)
    c: Coincident(g188,g178)
    c: Coincident(g188,g13)
    c: Vertical(g188)
    c: Coincident(g189,g19)
    c: Coincident(g189,g172)
    c: Vertical(g189)
    c: Coincident(g190,g172)
    c: Coincident(g190,g166)
    c: Horizontal(g190)
    c: Coincident(g191,g166)
    c: Coincident(g191,g19)
    c: Coincident(g192,g13)
    c: Weight(g193) = 1
    c: Equal(g193,g194)
    c: Equal(g193,g195)
    c: InternalAlignment(g193,g196)
    c: InternalAlignment(g194,g196)
    c: InternalAlignment(g195,g196)
    c: InternalAlignment(g197,g196)
    c: InternalAlignment(g198,g196)
    c: Weight(g199) = 1
    c: Equal(g199,g200)
    c: Equal(g199,g201)
    c: InternalAlignment(g199,g202)
    c: InternalAlignment(g200,g202)
    c: InternalAlignment(g201,g202)
    c: InternalAlignment(g203,g202)
    c: InternalAlignment(g204,g202)
    c: Block(g202)
    c: Block(g196)
    c: Coincident(g205,g202)
    c: Coincident(g205,g37)
    c: Coincident(g206,g37)
    c: Coincident(g206,g196)
    c: Coincident(g207,g196)
    c: Coincident(g207,g202)
    c: Vertical(g207)
    c: Weight(g208) = 1
    c: Equal(g208,g209)
    c: Equal(g208,g210)
    c: InternalAlignment(g208,g211)
    c: InternalAlignment(g209,g211)
    c: InternalAlignment(g210,g211)
    c: InternalAlignment(g212,g211)
    c: InternalAlignment(g213,g211)
    c: Weight(g214) = 1
    c: Equal(g214,g215)
    c: Equal(g214,g216)
    c: InternalAlignment(g214,g217)
    c: InternalAlignment(g215,g217)
    c: InternalAlignment(g216,g217)
    c: InternalAlignment(g218,g217)
    c: InternalAlignment(g219,g217)
    c: Block(g217)
    c: Block(g211)
    c: Coincident(g220,g211)
    c: Coincident(g220,g43)
    c: Coincident(g221,g43)
    c: Coincident(g221,g217)
    c: Coincident(g222,g217)
    c: Coincident(g222,g211)
    c: Vertical(g222)
    c: Horizontal(g223)
    c: Block(g223)
    c: Vertical(g224)
    c: Block(g224)
    c: Block(g225)
    c: Weight(g226) = 1
    c: Equal(g226,g227)
    c: Equal(g226,g228)
    c: InternalAlignment(g226,g229)
    c: InternalAlignment(g227,g229)
    c: InternalAlignment(g228,g229)
    c: InternalAlignment(g230,g229)
    c: InternalAlignment(g231,g229)
    c: Weight(g232) = 1
    c: Equal(g232,g233)
    c: Equal(g232,g234)
    c: InternalAlignment(g232,g235)
    c: InternalAlignment(g233,g235)
    c: InternalAlignment(g234,g235)
    c: InternalAlignment(g236,g235)
    c: InternalAlignment(g237,g235)
    c: Weight(g238) = 1
    c: Equal(g238,g239)
    c: Equal(g238,g240)
    c: InternalAlignment(g238,g241)
    c: InternalAlignment(g239,g241)
    c: InternalAlignment(g240,g241)
    c: InternalAlignment(g242,g241)
    c: InternalAlignment(g243,g241)
    c: Weight(g244) = 1
    c: Equal(g244,g245)
    c: Equal(g244,g246)
    c: InternalAlignment(g244,g247)
    c: InternalAlignment(g245,g247)
    c: InternalAlignment(g246,g247)
    c: InternalAlignment(g248,g247)
    c: InternalAlignment(g249,g247)
    c: Block(g229)
    c: Block(g235)
    c: Block(g241)
    c: Block(g247)
    c: Coincident(g250,g235)
    c: Coincident(g250,g229)
    c: Horizontal(g250)
    c: Block(g192)
    c: Weight(g251) = 1
    c: Equal(g251,g252)
    c: Equal(g251,g253)
    c: InternalAlignment(g251,g254)
    c: InternalAlignment(g252,g254)
    c: InternalAlignment(g253,g254)
    c: InternalAlignment(g255,g254)
    c: InternalAlignment(g256,g254)
    c: Weight(g257) = 1
    c: Equal(g257,g258)
    c: Equal(g257,g259)
    c: InternalAlignment(g257,g260)
    c: InternalAlignment(g258,g260)
    c: InternalAlignment(g259,g260)
    c: InternalAlignment(g261,g260)
    c: InternalAlignment(g262,g260)
    c: Block(g254)
    c: Block(g260)
    c: Coincident(g263,g254)
    c: Coincident(g263,g260)
    c: Weight(g264) = 1
    c: Equal(g264,g265)
    c: Equal(g264,g266)
    c: InternalAlignment(g264,g267)
    c: InternalAlignment(g265,g267)
    c: InternalAlignment(g266,g267)
    c: InternalAlignment(g268,g267)
    c: InternalAlignment(g269,g267)
    c: Weight(g270) = 1
    c: Equal(g270,g271)
    c: Equal(g270,g272)
    c: InternalAlignment(g270,g273)
    c: InternalAlignment(g271,g273)
    c: InternalAlignment(g272,g273)
    c: InternalAlignment(g274,g273)
    c: InternalAlignment(g275,g273)
    c: Weight(g276) = 1
    c: Equal(g276,g277)
    c: Equal(g276,g278)
    c: InternalAlignment(g276,g279)
    c: InternalAlignment(g277,g279)
    c: InternalAlignment(g278,g279)
    c: InternalAlignment(g280,g279)
    c: InternalAlignment(g281,g279)
    c: Block(g279)
    c: Block(g273)
    c: Block(g267)
    c: Coincident(g282,g273)
    c: Coincident(g282,g267)
    c: Coincident(g283,g267)
    c: Coincident(g283,g279)
    c: Vertical(g283)
    c: Coincident(g284,g279)
    c: Coincident(g284,g273)
    c: Horizontal(g284)
    c: Weight(g285) = 1
    c: Equal(g285,g286)
    c: InternalAlignment(g285,g287)
    c: InternalAlignment(g286,g287)
    c: InternalAlignment(g288,g287)
    c: InternalAlignment(g289,g287)
    c: Weight(g290) = 1
    c: InternalAlignment(g291,g293)
    c: InternalAlignment(g292,g293)
    c: InternalAlignment(g294,g293)
    c: InternalAlignment(g295,g293)
    c: Weight(g296) = 1
    c: Equal(g296,g297)
    c: Equal(g296,g298)
    c: InternalAlignment(g296,g299)
    c: InternalAlignment(g297,g299)
    c: InternalAlignment(g298,g299)
    c: InternalAlignment(g300,g299)
    c: InternalAlignment(g301,g299)
    c: Equal(g302,g303)
    c: Equal(g302,g304)
    c: InternalAlignment(g302,g305)
    c: InternalAlignment(g303,g305)
    c: InternalAlignment(g304,g305)
    c: InternalAlignment(g306,g305)
    c: InternalAlignment(g307,g305)
    c: Block(g293)
    c: Block(g299)
    c: Block(g305)
    c: Block(g287)
    c: Coincident(g308,g287)
    c: Coincident(g308,g293)
    c: Horizontal(g308)
    c: Coincident(g309,g293)
    c: Coincident(g309,g299)
    c: Vertical(g309)
    c: Coincident(g310,g299)
    c: Coincident(g310,g305)
    c: Horizontal(g310)
    c: Coincident(g311,g305)
    c: Coincident(g311,g287)
    c: Weight(g312) = 1
    c: Equal(g312,g313)
    c: Equal(g312,g314)
    c: InternalAlignment(g312,g315)
    c: InternalAlignment(g313,g315)
    c: InternalAlignment(g314,g315)
    c: InternalAlignment(g316,g315)
    c: InternalAlignment(g317,g315)
    c: Weight(g318) = 1
    c: Equal(g318,g319)
    c: Equal(g318,g320)
    c: InternalAlignment(g318,g321)
    c: InternalAlignment(g319,g321)
    c: InternalAlignment(g320,g321)
    c: InternalAlignment(g322,g321)
    c: InternalAlignment(g323,g321)
    c: Weight(g324) = 1
    c: Equal(g324,g325)
    c: Equal(g324,g326)
    c: InternalAlignment(g324,g327)
    c: InternalAlignment(g325,g327)
    c: InternalAlignment(g326,g327)
    c: InternalAlignment(g328,g327)
    c: InternalAlignment(g329,g327)
    c: Block(g327)
    c: Block(g321)
    c: Block(g315)
    c: Coincident(g330,g327)
    c: Coincident(g330,g321)
    c: Horizontal(g330)
    c: Coincident(g331,g321)
    c: Coincident(g331,g315)
    c: Vertical(g331)
    c: Coincident(g332,g315)
    c: Coincident(g332,g327)
    c: InternalAlignment(g333,g334)
    c: InternalAlignment(g335,g334)
    c: InternalAlignment(g336,g334)
    c: Block(g334)
    c: Equal(g337,g338)
    c: Equal(g337,g339)
    c: InternalAlignment(g337,g340)
    c: InternalAlignment(g338,g340)
    c: InternalAlignment(g339,g340)
    c: InternalAlignment(g341,g340)
    c: InternalAlignment(g342,g340)
    c: Block(g340)
    c: Coincident(g343,g334)
    c: Horizontal(g343)
    c: Block(g343)
    c: Coincident(g344,g334)
    c: Coincident(g344,g260)
    c: Vertical(g344)
    c: Coincident(g345,g340)
    c: Coincident(g345,g254)
    c: Vertical(g345)
    c: Coincident(g347,g5)
    c: Coincident(g348,g5)
    c: Block(g346)
    c: Block(g5)
    c: Block(g348)
    c: Block(g347)
    c: Distance(g344) = 119.89
FEATURE [Sketcher::SketchObject] Sketch001
  FullyConstrained = true
  MapMode = 4
  Placement = pos=(0,0,0) rot=(0.57735,0.57735,0.57735;2.0944rad)
  Support = -> [Sketch]
  sketch-geometry (46):
    g0: BSplineCurve PolesCount=3 KnotsCount=2 Degree=2 IsPeriodic=0
    g1: ArcOfCircle CenterX=73.1223 CenterY=-32.291 CenterZ=0 NormalX=0 NormalY=0 NormalZ=1 AngleXU=0 Radius=13 StartAngle=5.92268 EndAngle=9.06428
    g2: ArcOfCircle CenterX=66.7816 CenterY=-49.1439 CenterZ=0 NormalX=0 NormalY=0 NormalZ=1 AngleXU=0 Radius=13 StartAngle=2.78068 EndAngle=5.92131
    g3: ArcOfCircle CenterX=55.9263 CenterY=-78.1807 CenterZ=0 NormalX=0 NormalY=0 NormalZ=1 AngleXU=0 Radius=13 StartAngle=5.92268 EndAngle=9.06428
    g4: ArcOfCircle CenterX=49.5884 CenterY=-95.0342 CenterZ=0 NormalX=0 NormalY=0 NormalZ=1 AngleXU=0 Radius=13 StartAngle=2.78068 EndAngle=5.92131
    g5: ArcOfCircle CenterX=38.7206 CenterY=-124.067 CenterZ=0 NormalX=0 NormalY=0 NormalZ=1 AngleXU=0 Radius=13 StartAngle=5.92268 EndAngle=9.06428
    g6: ArcOfCircle CenterX=32.3875 CenterY=-140.92 CenterZ=0 NormalX=0 NormalY=0 NormalZ=1 AngleXU=0 Radius=13 StartAngle=2.78068 EndAngle=5.92131
    g7: ArcOfCircle CenterX=21.4715 CenterY=-169.934 CenterZ=0 NormalX=0 NormalY=0 NormalZ=1 AngleXU=0 Radius=13 StartAngle=5.92268 EndAngle=9.06428
    g8: ArcOfCircle CenterX=15.1336 CenterY=-186.787 CenterZ=0 NormalX=0 NormalY=0 NormalZ=1 AngleXU=0 Radius=13 StartAngle=2.78068 EndAngle=5.92131
    g9-g12: Circle x4 (B-spline internal-alignment scaffolding for g13; pole/knot coordinates omitted)
    g13: BSplineCurve PolesCount=4 KnotsCount=2 Degree=3 IsPeriodic=0
    g14: GeomPoint X=28.8094 Y=-19.0875 Z=0
    g15: GeomPoint X=47.0443 Y=-50.4712 Z=0
    g16: Circle CenterX=53.5586 CenterY=-23.2695 CenterZ=0 NormalX=0 NormalY=0 NormalZ=1 AngleXU=0 Radius=3.24518
    g17: Circle CenterX=-195.441 CenterY=-127.082 CenterZ=0 NormalX=0 NormalY=0 NormalZ=1 AngleXU=0 Radius=1
    g18: Circle CenterX=-8.24091 CenterY=-197.481 CenterZ=0 NormalX=0 NormalY=0 NormalZ=1 AngleXU=0 Radius=1
    g19: Circle CenterX=12.8789 CenterY=-141.321 CenterZ=0 NormalX=0 NormalY=0 NormalZ=1 AngleXU=0 Radius=1
    g20: BSplineCurve PolesCount=3 KnotsCount=2 Degree=2 IsPeriodic=0
    g21: GeomPoint X=-195.441 Y=-127.082 Z=0
    g22: GeomPoint X=12.8789 Y=-141.321 Z=0
    g23: Circle CenterX=-12.8016 CenterY=-179.036 CenterZ=0 NormalX=0 NormalY=0 NormalZ=1 AngleXU=0 Radius=10.5072
    g24: Circle CenterX=0.933922 CenterY=-166.43 CenterZ=0 NormalX=0 NormalY=0 NormalZ=1 AngleXU=0 Radius=3.26661
    g25: Circle CenterX=-33.5518 CenterY=-176.44 CenterZ=0 NormalX=0 NormalY=0 NormalZ=1 AngleXU=0 Radius=5.64388
    g26: Circle CenterX=-47.2366 CenterY=-173.859 CenterZ=0 NormalX=0 NormalY=0 NormalZ=1 AngleXU=0 Radius=3.01653
    g27: Circle CenterX=-56.2595 CenterY=-171.456 CenterZ=0 NormalX=0 NormalY=0 NormalZ=1 AngleXU=0 Radius=2.12826
    g28: ArcOfCircle CenterX=51.2151 CenterY=-198.473 CenterZ=0 NormalX=0 NormalY=0 NormalZ=1 AngleXU=0 Radius=20 StartAngle=2.78189 EndAngle=4.35269
    g29: LineSegment StartX=32.4951 StartY=-191.433 StartZ=0 EndX=94.6578 EndY=-26.1352 EndZ=0
    g30: LineSegment StartX=43.1192 StartY=-220.001 StartZ=0 EndX=-196.497 EndY=-129.89 EndZ=0
    g31: LineSegment StartX=43.1192 StartY=-220.001 StartZ=0 EndX=44.1752 EndY=-217.193 EndZ=0
    g32: LineSegment StartX=117.223 StartY=-19.0875 StartZ=0 EndX=117.223 EndY=-16.0875 EndZ=0
    g33: LineSegment StartX=117.223 StartY=-16.0875 StartZ=0 EndX=17.2232 EndY=-16.0875 EndZ=0
    g34: LineSegment StartX=17.2232 StartY=-16.0875 StartZ=0 EndX=17.2232 EndY=-19.0875 EndZ=0
    g35: LineSegment StartX=28.8094 StartY=-19.0875 StartZ=0 EndX=17.2232 EndY=-19.0875 EndZ=0
    g36: LineSegment StartX=47.0443 StartY=-50.4712 StartZ=0 EndX=12.8789 EndY=-141.321 EndZ=0
    g37: LineSegment StartX=-195.441 StartY=-127.082 StartZ=0 EndX=-196.497 EndY=-129.89 EndZ=0
    g38: LineSegment StartX=85.2866 StartY=-36.8766 StartZ=0 EndX=78.9396 EndY=-53.7463 EndZ=0
    g39: LineSegment StartX=60.9579 StartY=-27.7053 StartZ=0 EndX=54.6191 EndY=-44.5532 EndZ=0
    g40: LineSegment StartX=68.0907 StartY=-82.7664 StartZ=0 EndX=61.7465 EndY=-99.6365 EndZ=0
    g41: LineSegment StartX=43.7619 StartY=-73.595 StartZ=0 EndX=37.426 EndY=-90.4435 EndZ=0
    g42: LineSegment StartX=50.885 StartY=-128.652 StartZ=0 EndX=44.5456 EndY=-145.522 EndZ=0
    g43: LineSegment StartX=26.5562 StartY=-119.481 StartZ=0 EndX=20.2251 EndY=-136.329 EndZ=0
    g44: LineSegment StartX=9.3071 StartY=-165.349 StartZ=0 EndX=2.97115 EndY=-182.197 EndZ=0
    g45: LineSegment StartX=33.6358 StartY=-174.52 StartZ=0 EndX=27.2917 EndY=-191.39 EndZ=0
  constraints (71):
    c: Block(g0)
    c: Block(g1)
    c: Block(g2)
    c: Block(g4)
    c: Block(g3)
    c: Block(g6)
    c: Block(g5)
    c: Block(g8)
    c: Block(g7)
    c: Weight(g9) = 1
    c: Equal(g9,g10)
    c: Equal(g9,g11)
    c: Equal(g9,g12)
    c: InternalAlignment(g9-g12 -> g13) x4
    c: InternalAlignment(g14,g13)
    c: InternalAlignment(g15,g13)
    c: Block(g16)
    c: Weight(g17) = 1
    c: Equal(g17,g18)
    c: Equal(g17,g19)
    c: InternalAlignment(g17,g20)
    c: InternalAlignment(g18,g20)
    c: InternalAlignment(g19,g20)
    c: InternalAlignment(g21,g20)
    c: InternalAlignment(g22,g20)
    c: Block(g20)
    c: Block(g23)
    c: Block(g24)
    c: Block(g25)
    c: Block(g26)
    c: Block(g27)
    c: Block(g28)
    c: Coincident(g29,g28)
    c: Coincident(g29,g0)
    c: Block(g13)
    c: Coincident(g31,g30)
    c: Coincident(g31,g28)
    c: Block(g31)
    c: Coincident(g32,g0)
    c: Vertical(g32)
    c: Coincident(g33,g32)
    c: Horizontal(g33)
    c: Coincident(g34,g33)
    c: Vertical(g34)
    c: Block(g33)
    c: Coincident(g35,g13)
    c: Coincident(g35,g34)
    c: Horizontal(g35)
    c: Coincident(g36,g13)
    c: Coincident(g36,g20)
    c: Coincident(g37,g20)
    c: Coincident(g37,g30)
    c: Block(g30)
    c: Coincident(g38,g1)
    c: Coincident(g38,g2)
    c: Coincident(g39,g1)
    c: Coincident(g39,g2)
    c: Coincident(g40,g3)
    c: Coincident(g40,g4)
    c: Coincident(g41,g3)
    c: Coincident(g41,g4)
    c: Coincident(g42,g5)
    c: Coincident(g42,g6)
    c: Coincident(g43,g5)
    c: Coincident(g43,g6)
    c: Coincident(g44,g7)
    c: Coincident(g44,g8)
    c: Coincident(g45,g7)
    c: Coincident(g45,g8)
    c: Distance(g30) = 256
    c: Distance(g33) = 100
FEATURE [Part::Extrusion] Extrude002
  Base = -> Sketch001
  Dir = (1,0,0)
  DirMode = 2
  FaceMakerClass = Part::FaceMakerBullseye
  LengthFwd = 8
  LengthRev = 0
  Solid = true
  Symmetric = false
FEATURE [Sketcher::SketchObject] Sketch002
  FullyConstrained = true
  sketch-geometry (20):
    g0: LineSegment StartX=-2.77179 StartY=-200.304 StartZ=0 EndX=5.22821 EndY=-200.304 EndZ=0
    g1: LineSegment StartX=5.22821 StartY=-200.304 StartZ=0 EndX=5.22821 EndY=-197.304 EndZ=0
    g2: LineSegment StartX=-2.77179 StartY=-200.304 StartZ=0 EndX=-2.77179 EndY=-197.304 EndZ=0
    g3: LineSegment StartX=5.22821 StartY=-197.304 StartZ=0 EndX=8.22821 EndY=-197.304 EndZ=0
    g4: LineSegment StartX=-2.77179 StartY=-197.304 StartZ=0 EndX=-5.77179 EndY=-197.304 EndZ=0
    g5: LineSegment StartX=19.2282 StartY=-203.304 StartZ=0 EndX=19.2282 EndY=-206.304 EndZ=0
    g6: LineSegment StartX=-16.7718 StartY=-203.304 StartZ=0 EndX=-16.7718 EndY=-206.304 EndZ=0
    g7: LineSegment StartX=-16.7718 StartY=-206.304 StartZ=0 EndX=19.2282 EndY=-206.304 EndZ=0
    g8: Circle CenterX=-16.7718 CenterY=-203.304 CenterZ=0 NormalX=0 NormalY=0 NormalZ=1 AngleXU=0 Radius=1
    g9: Circle CenterX=-5.77179 CenterY=-203.304 CenterZ=0 NormalX=0 NormalY=0 NormalZ=1 AngleXU=0 Radius=1
    g10: Circle CenterX=-5.77179 CenterY=-197.304 CenterZ=0 NormalX=0 NormalY=0 NormalZ=1 AngleXU=0 Radius=1
    g11: BSplineCurve PolesCount=3 KnotsCount=2 Degree=2 IsPeriodic=0
    g12: GeomPoint X=-16.7718 Y=-203.304 Z=0
    g13: GeomPoint X=-5.77179 Y=-197.304 Z=0
    g14: Circle CenterX=19.2282 CenterY=-203.304 CenterZ=0 NormalX=0 NormalY=0 NormalZ=1 AngleXU=0 Radius=1
    g15: Circle CenterX=8.22821 CenterY=-203.304 CenterZ=0 NormalX=0 NormalY=0 NormalZ=1 AngleXU=0 Radius=1
    g16: Circle CenterX=8.22821 CenterY=-197.304 CenterZ=0 NormalX=0 NormalY=0 NormalZ=1 AngleXU=0 Radius=1
    g17: BSplineCurve PolesCount=3 KnotsCount=2 Degree=2 IsPeriodic=0
    g18: GeomPoint X=19.2282 Y=-203.304 Z=0
    g19: GeomPoint X=8.22821 Y=-197.304 Z=0
  constraints (41):
    c: Horizontal(g0)
    c: Distance(g0) = 8
    c: Coincident(g1,g0)
    c: Vertical(g1)
    c: Distance(g1) = 3
    c: Coincident(g2,g0)
    c: Vertical(g2)
    c: Distance(g2) = 3
    c: Coincident(g3,g1)
    c: Horizontal(g3)
    c: Distance(g3) = 3
    c: Coincident(g4,g2)
    c: Horizontal(g4)
    c: Distance(g4) = 3
    c: Vertical(g5)
    c: Vertical(g6)
    c: Coincident(g7,g6)
    c: Coincident(g7,g5)
    c: Weight(g8) = 1
    c: Equal(g8,g9)
    c: Equal(g8,g10)
    c: Coincident(g11,g4)
    c: InternalAlignment(g8,g11)
    c: InternalAlignment(g9,g11)
    c: InternalAlignment(g10,g11)
    c: InternalAlignment(g12,g11)
    c: InternalAlignment(g13,g11)
    c: Coincident(g17,g5)
    c: Weight(g14) = 1
    c: Equal(g14,g15)
    c: Equal(g14,g16)
    c: Coincident(g17,g3)
    c: InternalAlignment(g14,g17)
    c: InternalAlignment(g15,g17)
    c: InternalAlignment(g16,g17)
    c: InternalAlignment(g18,g17)
    c: InternalAlignment(g19,g17)
    c: Block(g7)
    c: Block(g17)
    c: Block(g11)
    c: Block(g6)
FEATURE [Part::Extrusion] Extrude003
  Base = -> Sketch002
  Dir = (0,0,1)
  DirMode = 2
  FaceMakerClass = Part::FaceMakerBullseye
  LengthFwd = 260
  LengthRev = 0
  Solid = true
  Symmetric = false
FEATURE [Sketcher::SketchObject] Sketch003
  FullyConstrained = false
  sketch-geometry (415):
    g0: LineSegment StartX=-42.9272 StartY=136.221 StartZ=0 EndX=-42.9272 EndY=-103.779 EndZ=0
    g1: LineSegment StartX=407.073 StartY=136.221 StartZ=0 EndX=407.073 EndY=-103.779 EndZ=0
    g2: ArcOfCircle CenterX=-26.9272 CenterY=-83.7794 CenterZ=0 NormalX=0 NormalY=0 NormalZ=1 AngleXU=0 Radius=8 StartAngle=3.14159 EndAngle=6.28319
    g3: ArcOfCircle CenterX=391.073 CenterY=-83.7794 CenterZ=0 NormalX=0 NormalY=0 NormalZ=1 AngleXU=0 Radius=8 StartAngle=3.14159 EndAngle=6.28319
    g4: Circle CenterX=175.022 CenterY=27.0628 CenterZ=0 NormalX=0 NormalY=0 NormalZ=1 AngleXU=0 Radius=1
    g5: Circle CenterX=179.022 CenterY=24.8665 CenterZ=0 NormalX=0 NormalY=0 NormalZ=1 AngleXU=0 Radius=1
    g6: Circle CenterX=179.022 CenterY=27.0628 CenterZ=0 NormalX=0 NormalY=0 NormalZ=1 AngleXU=0 Radius=1
    g7: BSplineCurve PolesCount=3 KnotsCount=2 Degree=2 IsPeriodic=0
    g8: GeomPoint X=175.022 Y=27.0628 Z=0
    g9: GeomPoint X=179.022 Y=27.0628 Z=0
    g10: Circle CenterX=189.124 CenterY=27.0628 CenterZ=0 NormalX=0 NormalY=0 NormalZ=1 AngleXU=0 Radius=1
    g11: Circle CenterX=185.124 CenterY=24.8665 CenterZ=0 NormalX=0 NormalY=0 NormalZ=1 AngleXU=0 Radius=1
    g12: Circle CenterX=185.124 CenterY=27.0628 CenterZ=0 NormalX=0 NormalY=0 NormalZ=1 AngleXU=0 Radius=1
    g13: BSplineCurve PolesCount=3 KnotsCount=2 Degree=2 IsPeriodic=0
    g14: GeomPoint X=189.124 Y=27.0628 Z=0
    g15: GeomPoint X=185.124 Y=27.0628 Z=0
    g16: Circle CenterX=175.022 CenterY=5.37834 CenterZ=0 NormalX=0 NormalY=0 NormalZ=1 AngleXU=0 Radius=1
    g17: Circle CenterX=179.022 CenterY=7.57463 CenterZ=0 NormalX=0 NormalY=0 NormalZ=1 AngleXU=0 Radius=1
    g18: Circle CenterX=179.022 CenterY=5.34704 CenterZ=0 NormalX=0 NormalY=0 NormalZ=1 AngleXU=0 Radius=1
    g19: BSplineCurve PolesCount=3 KnotsCount=2 Degree=2 IsPeriodic=0
    g20: GeomPoint X=175.022 Y=5.37834 Z=0
    g21: GeomPoint X=179.022 Y=5.34704 Z=0
    g22: Circle CenterX=189.124 CenterY=5.37834 CenterZ=0 NormalX=0 NormalY=0 NormalZ=1 AngleXU=0 Radius=1
    g23: Circle CenterX=185.124 CenterY=7.57463 CenterZ=0 NormalX=0 NormalY=0 NormalZ=1 AngleXU=0 Radius=1
    g24: Circle CenterX=185.124 CenterY=5.34704 CenterZ=0 NormalX=0 NormalY=0 NormalZ=1 AngleXU=0 Radius=1
    g25: BSplineCurve PolesCount=3 KnotsCount=2 Degree=2 IsPeriodic=0
    g26: GeomPoint X=189.124 Y=5.37834 Z=0
    g27: GeomPoint X=185.124 Y=5.34704 Z=0
    g28: Circle CenterX=165.871 CenterY=18.1458 CenterZ=0 NormalX=0 NormalY=0 NormalZ=1 AngleXU=0 Radius=1
    g29: Circle CenterX=169.377 CenterY=16.2206 CenterZ=0 NormalX=0 NormalY=0 NormalZ=1 AngleXU=0 Radius=1
    g30: Circle CenterX=165.871 CenterY=14.2954 CenterZ=0 NormalX=0 NormalY=0 NormalZ=1 AngleXU=0 Radius=1
    g31: BSplineCurve PolesCount=3 KnotsCount=2 Degree=2 IsPeriodic=0
    g32: GeomPoint X=165.871 Y=18.1458 Z=0
    g33: GeomPoint X=165.871 Y=14.2954 Z=0
    g34: Circle CenterX=198.275 CenterY=18.1458 CenterZ=0 NormalX=0 NormalY=0 NormalZ=1 AngleXU=0 Radius=1
    g35: Circle CenterX=194.768 CenterY=16.2206 CenterZ=0 NormalX=0 NormalY=0 NormalZ=1 AngleXU=0 Radius=1
    g36: Circle CenterX=198.275 CenterY=14.2954 CenterZ=0 NormalX=0 NormalY=0 NormalZ=1 AngleXU=0 Radius=1
    g37: BSplineCurve PolesCount=3 KnotsCount=2 Degree=2 IsPeriodic=0
    g38: GeomPoint X=198.275 Y=18.1458 Z=0
    g39: GeomPoint X=198.275 Y=14.2954 Z=0
    g40: LineSegment StartX=407.073 StartY=-103.779 StartZ=0 EndX=-42.9272 EndY=-103.779 EndZ=0
    g41: Circle CenterX=125.607 CenterY=54.1951 CenterZ=0 NormalX=0 NormalY=0 NormalZ=1 AngleXU=0 Radius=1
    g42: Circle CenterX=139.632 CenterY=46.4944 CenterZ=0 NormalX=0 NormalY=0 NormalZ=1 AngleXU=0 Radius=1
    g43: Circle CenterX=127.326 CenterY=56.7187 CenterZ=0 NormalX=0 NormalY=0 NormalZ=1 AngleXU=0 Radius=1
    g44: BSplineCurve PolesCount=3 KnotsCount=2 Degree=2 IsPeriodic=0
    g45: GeomPoint X=125.607 Y=54.1951 Z=0
    g46: GeomPoint X=127.326 Y=56.7187 Z=0
    g47: Circle CenterX=236.821 CenterY=56.7187 CenterZ=0 NormalX=0 NormalY=0 NormalZ=1 AngleXU=0 Radius=1
    g48: Circle CenterX=224.513 CenterY=46.4944 CenterZ=0 NormalX=0 NormalY=0 NormalZ=1 AngleXU=0 Radius=1
    g49: Circle CenterX=238.538 CenterY=54.1951 CenterZ=0 NormalX=0 NormalY=0 NormalZ=1 AngleXU=0 Radius=1
    g50: BSplineCurve PolesCount=3 KnotsCount=2 Degree=2 IsPeriodic=0
    g51: GeomPoint X=236.821 Y=56.7187 Z=0
    g52: GeomPoint X=238.538 Y=54.1951 Z=0
    g53: Circle CenterX=238.538 CenterY=-21.7539 CenterZ=0 NormalX=0 NormalY=0 NormalZ=1 AngleXU=0 Radius=1
    g54: Circle CenterX=224.513 CenterY=-14.0532 CenterZ=0 NormalX=0 NormalY=0 NormalZ=1 AngleXU=0 Radius=1
    g55: Circle CenterX=236.821 CenterY=-24.2775 CenterZ=0 NormalX=0 NormalY=0 NormalZ=1 AngleXU=0 Radius=1
    g56: BSplineCurve PolesCount=3 KnotsCount=2 Degree=2 IsPeriodic=0
    g57: GeomPoint X=238.538 Y=-21.7539 Z=0
    g58: GeomPoint X=236.821 Y=-24.2775 Z=0
    g59: Circle CenterX=125.607 CenterY=-21.7539 CenterZ=0 NormalX=0 NormalY=0 NormalZ=1 AngleXU=0 Radius=1
    g60: Circle CenterX=139.632 CenterY=-14.0532 CenterZ=0 NormalX=0 NormalY=0 NormalZ=1 AngleXU=0 Radius=1
    g61: Circle CenterX=127.325 CenterY=-24.2775 CenterZ=0 NormalX=0 NormalY=0 NormalZ=1 AngleXU=0 Radius=1
    g62: BSplineCurve PolesCount=3 KnotsCount=2 Degree=2 IsPeriodic=0
    g63: GeomPoint X=125.607 Y=-21.7539 Z=0
    g64: GeomPoint X=127.325 Y=-24.2775 Z=0
    g65: Circle CenterX=302.996 CenterY=111.695 CenterZ=0 NormalX=0 NormalY=0 NormalZ=1 AngleXU=0 Radius=1
    g66: Circle CenterX=306.073 CenterY=114.251 CenterZ=0 NormalX=0 NormalY=0 NormalZ=1 AngleXU=0 Radius=1
    g67: Circle CenterX=306.073 CenterY=110.251 CenterZ=0 NormalX=0 NormalY=0 NormalZ=1 AngleXU=0 Radius=1
    g68: BSplineCurve PolesCount=3 KnotsCount=2 Degree=2 IsPeriodic=0
    g69: GeomPoint X=302.996 Y=111.695 Z=0
    g70: GeomPoint X=306.073 Y=110.251 Z=0
    g71: Circle CenterX=306.073 CenterY=95.2763 CenterZ=0 NormalX=0 NormalY=0 NormalZ=1 AngleXU=0 Radius=1
    g72: Circle CenterX=306.073 CenterY=91.2763 CenterZ=0 NormalX=0 NormalY=0 NormalZ=1 AngleXU=0 Radius=1
    g73: Circle CenterX=302.567 CenterY=89.3511 CenterZ=0 NormalX=0 NormalY=0 NormalZ=1 AngleXU=0 Radius=1
    g74: BSplineCurve PolesCount=3 KnotsCount=2 Degree=2 IsPeriodic=0
    g75: GeomPoint X=306.073 Y=95.2763 Z=0
    g76: GeomPoint X=302.567 Y=89.3511 Z=0
    g77: LineSegment StartX=306.073 StartY=110.251 StartZ=0 EndX=306.073 EndY=95.2763 EndZ=0
    g78: LineSegment StartX=302.996 StartY=111.695 StartZ=0 EndX=236.821 EndY=56.7187 EndZ=0
    g79: LineSegment StartX=238.538 StartY=54.1951 StartZ=0 EndX=302.567 EndY=89.3511 EndZ=0
    g80: Circle CenterX=61.1496 CenterY=111.695 CenterZ=0 NormalX=0 NormalY=0 NormalZ=1 AngleXU=0 Radius=1
    g81: Circle CenterX=58.0728 CenterY=114.251 CenterZ=0 NormalX=0 NormalY=0 NormalZ=1 AngleXU=0 Radius=1
    g82: Circle CenterX=58.0728 CenterY=110.251 CenterZ=0 NormalX=0 NormalY=0 NormalZ=1 AngleXU=0 Radius=1
    g83: BSplineCurve PolesCount=3 KnotsCount=2 Degree=2 IsPeriodic=0
    g84: GeomPoint X=61.1496 Y=111.695 Z=0
    g85: GeomPoint X=58.0728 Y=110.251 Z=0
    g86: Circle CenterX=61.5791 CenterY=89.3511 CenterZ=0 NormalX=0 NormalY=0 NormalZ=1 AngleXU=0 Radius=1
    g87: Circle CenterX=58.0728 CenterY=91.2763 CenterZ=0 NormalX=0 NormalY=0 NormalZ=1 AngleXU=0 Radius=1
    g88: Circle CenterX=58.0728 CenterY=95.2763 CenterZ=0 NormalX=0 NormalY=0 NormalZ=1 AngleXU=0 Radius=1
    g89: BSplineCurve PolesCount=3 KnotsCount=2 Degree=2 IsPeriodic=0
    g90: GeomPoint X=61.5791 Y=89.3511 Z=0
    g91: GeomPoint X=58.0728 Y=95.2763 Z=0
    g92: LineSegment StartX=58.0728 StartY=110.251 StartZ=0 EndX=58.0728 EndY=95.2763 EndZ=0
    g93: LineSegment StartX=61.1496 StartY=111.695 StartZ=0 EndX=127.326 EndY=56.7187 EndZ=0
    g94: LineSegment StartX=125.607 StartY=54.1951 StartZ=0 EndX=61.5791 EndY=89.3511 EndZ=0
    g95: Circle CenterX=61.5791 CenterY=-56.9099 CenterZ=0 NormalX=0 NormalY=0 NormalZ=1 AngleXU=0 Radius=1
    g96: Circle CenterX=58.0728 CenterY=-58.8351 CenterZ=0 NormalX=0 NormalY=0 NormalZ=1 AngleXU=0 Radius=1
    g97: Circle CenterX=58.0728 CenterY=-62.8351 CenterZ=0 NormalX=0 NormalY=0 NormalZ=1 AngleXU=0 Radius=1
    g98: BSplineCurve PolesCount=3 KnotsCount=2 Degree=2 IsPeriodic=0
    g99: GeomPoint X=61.5791 Y=-56.9099 Z=0
    g100: GeomPoint X=58.0728 Y=-62.8351 Z=0
    g101: Circle CenterX=58.0728 CenterY=-77.8102 CenterZ=0 NormalX=0 NormalY=0 NormalZ=1 AngleXU=0 Radius=1
    g102: Circle CenterX=58.0728 CenterY=-81.8102 CenterZ=0 NormalX=0 NormalY=0 NormalZ=1 AngleXU=0 Radius=1
    g103: Circle CenterX=61.1496 CenterY=-79.2541 CenterZ=0 NormalX=0 NormalY=0 NormalZ=1 AngleXU=0 Radius=1
    g104: BSplineCurve PolesCount=3 KnotsCount=2 Degree=2 IsPeriodic=0
    g105: GeomPoint X=58.0728 Y=-77.8102 Z=0
    g106: GeomPoint X=61.1496 Y=-79.2541 Z=0
    g107: LineSegment StartX=58.0728 StartY=-62.8351 StartZ=0 EndX=58.0728 EndY=-77.8102 EndZ=0
    g108: LineSegment StartX=61.1496 StartY=-79.2541 StartZ=0 EndX=127.325 EndY=-24.2775 EndZ=0
    g109: LineSegment StartX=125.607 StartY=-21.7539 StartZ=0 EndX=61.5791 EndY=-56.9099 EndZ=0
    g110: Circle CenterX=302.567 CenterY=-56.9099 CenterZ=0 NormalX=0 NormalY=0 NormalZ=1 AngleXU=0 Radius=1
    g111: Circle CenterX=306.073 CenterY=-58.8351 CenterZ=0 NormalX=0 NormalY=0 NormalZ=1 AngleXU=0 Radius=1
    g112: Circle CenterX=306.073 CenterY=-62.8351 CenterZ=0 NormalX=0 NormalY=0 NormalZ=1 AngleXU=0 Radius=1
    g113: BSplineCurve PolesCount=3 KnotsCount=2 Degree=2 IsPeriodic=0
    g114: GeomPoint X=302.567 Y=-56.9099 Z=0
    g115: GeomPoint X=306.073 Y=-62.8351 Z=0
    g116: Circle CenterX=302.996 CenterY=-79.2541 CenterZ=0 NormalX=0 NormalY=0 NormalZ=1 AngleXU=0 Radius=1
    g117: Circle CenterX=306.073 CenterY=-81.8102 CenterZ=0 NormalX=0 NormalY=0 NormalZ=1 AngleXU=0 Radius=1
    g118: Circle CenterX=306.073 CenterY=-77.8102 CenterZ=0 NormalX=0 NormalY=0 NormalZ=1 AngleXU=0 Radius=1
    g119: BSplineCurve PolesCount=3 KnotsCount=2 Degree=2 IsPeriodic=0
    g120: GeomPoint X=302.996 Y=-79.2541 Z=0
    g121: GeomPoint X=306.073 Y=-77.8102 Z=0
    g122: LineSegment StartX=306.073 StartY=-62.8351 StartZ=0 EndX=306.073 EndY=-77.8102 EndZ=0
    g123: LineSegment StartX=302.996 StartY=-79.2541 StartZ=0 EndX=236.821 EndY=-24.2775 EndZ=0
    g124: LineSegment StartX=238.538 StartY=-21.7539 StartZ=0 EndX=302.567 EndY=-56.9099 EndZ=0
    g125: Circle CenterX=61.6457 CenterY=-88.8112 CenterZ=0 NormalX=0 NormalY=0 NormalZ=1 AngleXU=0 Radius=1
    g126: Circle CenterX=58.0728 CenterY=-91.7794 CenterZ=0 NormalX=0 NormalY=0 NormalZ=1 AngleXU=0 Radius=1
    g127: Circle CenterX=63.9135 CenterY=-91.7791 CenterZ=0 NormalX=0 NormalY=0 NormalZ=1 AngleXU=0 Radius=1
    g128: BSplineCurve PolesCount=3 KnotsCount=2 Degree=2 IsPeriodic=0
    g129: GeomPoint X=61.6457 Y=-88.8112 Z=0
    g130: GeomPoint X=63.9135 Y=-91.7791 Z=0
    g131: Circle CenterX=179.022 CenterY=-85.8163 CenterZ=0 NormalX=0 NormalY=0 NormalZ=1 AngleXU=0 Radius=1
    g132: Circle CenterX=179.022 CenterY=-91.7794 CenterZ=0 NormalX=0 NormalY=0 NormalZ=1 AngleXU=0 Radius=1
    g133: Circle CenterX=171.895 CenterY=-91.7791 CenterZ=0 NormalX=0 NormalY=0 NormalZ=1 AngleXU=0 Radius=1
    g134: BSplineCurve PolesCount=3 KnotsCount=2 Degree=2 IsPeriodic=0
    g135: GeomPoint X=179.022 Y=-85.8163 Z=0
    g136: GeomPoint X=171.895 Y=-91.7791 Z=0
    g137: Circle CenterX=185.124 CenterY=-86.2028 CenterZ=0 NormalX=0 NormalY=0 NormalZ=1 AngleXU=0 Radius=1
    g138: Circle CenterX=185.124 CenterY=-91.7794 CenterZ=0 NormalX=0 NormalY=0 NormalZ=1 AngleXU=0 Radius=1
    g139: Circle CenterX=191.747 CenterY=-91.7794 CenterZ=0 NormalX=0 NormalY=0 NormalZ=1 AngleXU=0 Radius=1
    g140: BSplineCurve PolesCount=3 KnotsCount=2 Degree=2 IsPeriodic=0
    g141: GeomPoint X=185.124 Y=-86.2028 Z=0
    g142: GeomPoint X=191.747 Y=-91.7794 Z=0
    g143: Circle CenterX=299.888 CenterY=-86.6413 CenterZ=0 NormalX=0 NormalY=0 NormalZ=1 AngleXU=0 Radius=1
    g144: Circle CenterX=306.073 CenterY=-91.7794 CenterZ=0 NormalX=0 NormalY=0 NormalZ=1 AngleXU=0 Radius=1
    g145: Circle CenterX=298.776 CenterY=-91.7794 CenterZ=0 NormalX=0 NormalY=0 NormalZ=1 AngleXU=0 Radius=1
    g146: BSplineCurve PolesCount=3 KnotsCount=2 Degree=2 IsPeriodic=0
    g147: GeomPoint X=299.888 Y=-86.6413 Z=0
    g148: GeomPoint X=298.776 Y=-91.7794 Z=0
    g149: LineSegment StartX=189.124 StartY=5.37834 StartZ=0 EndX=299.888 EndY=-86.6413 EndZ=0
    g150: LineSegment StartX=298.776 StartY=-91.7794 StartZ=0 EndX=191.747 EndY=-91.7794 EndZ=0
    g151: LineSegment StartX=185.124 StartY=-86.2028 StartZ=0 EndX=185.124 EndY=5.34704 EndZ=0
    g152: LineSegment StartX=179.022 StartY=5.34704 StartZ=0 EndX=179.022 EndY=-85.8163 EndZ=0
    g153: LineSegment StartX=171.895 StartY=-91.7791 StartZ=0 EndX=63.9135 EndY=-91.7791 EndZ=0
    g154: LineSegment StartX=61.6457 StartY=-88.8112 StartZ=0 EndX=175.022 EndY=5.37834 EndZ=0
    g155: Circle CenterX=302.073 CenterY=124.221 CenterZ=0 NormalX=0 NormalY=0 NormalZ=1 AngleXU=0 Radius=1
    g156: Circle CenterX=306.073 CenterY=124.221 CenterZ=0 NormalX=0 NormalY=0 NormalZ=1 AngleXU=0 Radius=1
    g157: Circle CenterX=302.996 CenterY=121.665 CenterZ=0 NormalX=0 NormalY=0 NormalZ=1 AngleXU=0 Radius=1
    g158: BSplineCurve PolesCount=3 KnotsCount=2 Degree=2 IsPeriodic=0
    g159: GeomPoint X=302.073 Y=124.221 Z=0
    g160: GeomPoint X=302.996 Y=121.665 Z=0
    g161: Circle CenterX=189.124 CenterY=124.221 CenterZ=0 NormalX=0 NormalY=0 NormalZ=1 AngleXU=0 Radius=1
    g162: Circle CenterX=185.124 CenterY=124.221 CenterZ=0 NormalX=0 NormalY=0 NormalZ=1 AngleXU=0 Radius=1
    g163: Circle CenterX=185.124 CenterY=120.221 CenterZ=0 NormalX=0 NormalY=0 NormalZ=1 AngleXU=0 Radius=1
    g164: BSplineCurve PolesCount=3 KnotsCount=2 Degree=2 IsPeriodic=0
    g165: GeomPoint X=189.124 Y=124.221 Z=0
    g166: GeomPoint X=185.124 Y=120.221 Z=0
    g167: Circle CenterX=175.022 CenterY=124.221 CenterZ=0 NormalX=0 NormalY=0 NormalZ=1 AngleXU=0 Radius=1
    g168: Circle CenterX=179.022 CenterY=124.221 CenterZ=0 NormalX=0 NormalY=0 NormalZ=1 AngleXU=0 Radius=1
    g169: Circle CenterX=179.022 CenterY=120.221 CenterZ=0 NormalX=0 NormalY=0 NormalZ=1 AngleXU=0 Radius=1
    g170: BSplineCurve PolesCount=3 KnotsCount=2 Degree=2 IsPeriodic=0
    g171: GeomPoint X=175.022 Y=124.221 Z=0
    g172: GeomPoint X=179.022 Y=120.221 Z=0
    g173: Circle CenterX=62.0728 CenterY=124.221 CenterZ=0 NormalX=0 NormalY=0 NormalZ=1 AngleXU=0 Radius=1
    g174: Circle CenterX=58.0728 CenterY=124.221 CenterZ=0 NormalX=0 NormalY=0 NormalZ=1 AngleXU=0 Radius=1
    g175: Circle CenterX=61.1496 CenterY=121.665 CenterZ=0 NormalX=0 NormalY=0 NormalZ=1 AngleXU=0 Radius=1
    g176: BSplineCurve PolesCount=3 KnotsCount=2 Degree=2 IsPeriodic=0
    g177: GeomPoint X=62.0728 Y=124.221 Z=0
    g178: GeomPoint X=61.1496 Y=121.665 Z=0
    g179: LineSegment StartX=179.022 StartY=120.221 StartZ=0 EndX=179.022 EndY=27.0628 EndZ=0
    g180: LineSegment StartX=185.124 StartY=27.0628 StartZ=0 EndX=185.124 EndY=120.221 EndZ=0
    g181: LineSegment StartX=302.996 StartY=121.665 StartZ=0 EndX=189.124 EndY=27.0628 EndZ=0
    g182: LineSegment StartX=175.022 StartY=27.0628 StartZ=0 EndX=61.1496 EndY=121.665 EndZ=0
    g183: Circle CenterX=61.5791 CenterY=75.4095 CenterZ=0 NormalX=0 NormalY=0 NormalZ=1 AngleXU=0 Radius=1
    g184: Circle CenterX=58.0728 CenterY=77.3346 CenterZ=0 NormalX=0 NormalY=0 NormalZ=1 AngleXU=0 Radius=1
    g185: Circle CenterX=58.0728 CenterY=73.3346 CenterZ=0 NormalX=0 NormalY=0 NormalZ=1 AngleXU=0 Radius=1
    g186: BSplineCurve PolesCount=3 KnotsCount=2 Degree=2 IsPeriodic=0
    g187: GeomPoint X=61.5791 Y=75.4095 Z=0
    g188: GeomPoint X=58.0728 Y=73.3346 Z=0
    g189: Circle CenterX=58.0728 CenterY=-40.8935 CenterZ=0 NormalX=0 NormalY=0 NormalZ=1 AngleXU=0 Radius=1
    g190: Circle CenterX=58.0728 CenterY=-44.8935 CenterZ=0 NormalX=0 NormalY=0 NormalZ=1 AngleXU=0 Radius=1
    g191: Circle CenterX=61.5791 CenterY=-42.9683 CenterZ=0 NormalX=0 NormalY=0 NormalZ=1 AngleXU=0 Radius=1
    g192: BSplineCurve PolesCount=3 KnotsCount=2 Degree=2 IsPeriodic=0
    g193: GeomPoint X=58.0728 Y=-40.8935 Z=0
    g194: GeomPoint X=61.5791 Y=-42.9683 Z=0
    g195: LineSegment StartX=61.5791 StartY=-42.9683 StartZ=0 EndX=165.871 EndY=14.2954 EndZ=0
    g196: LineSegment StartX=165.871 StartY=18.1458 StartZ=0 EndX=61.5791 EndY=75.4095 EndZ=0
    g197: LineSegment StartX=58.0728 StartY=73.3346 StartZ=0 EndX=58.0728 EndY=-40.8935 EndZ=0
    g198: Circle CenterX=302.567 CenterY=-42.9683 CenterZ=0 NormalX=0 NormalY=0 NormalZ=1 AngleXU=0 Radius=1
    g199: Circle CenterX=306.073 CenterY=-44.8935 CenterZ=0 NormalX=0 NormalY=0 NormalZ=1 AngleXU=0 Radius=1
    g200: Circle CenterX=306.073 CenterY=-40.8935 CenterZ=0 NormalX=0 NormalY=0 NormalZ=1 AngleXU=0 Radius=1
    g201: BSplineCurve PolesCount=3 KnotsCount=2 Degree=2 IsPeriodic=0
    g202: GeomPoint X=302.567 Y=-42.9683 Z=0
    g203: GeomPoint X=306.073 Y=-40.8935 Z=0
    g204: Circle CenterX=306.073 CenterY=73.3346 CenterZ=0 NormalX=0 NormalY=0 NormalZ=1 AngleXU=0 Radius=1
    g205: Circle CenterX=306.073 CenterY=77.3346 CenterZ=0 NormalX=0 NormalY=0 NormalZ=1 AngleXU=0 Radius=1
    g206: Circle CenterX=302.567 CenterY=75.4095 CenterZ=0 NormalX=0 NormalY=0 NormalZ=1 AngleXU=0 Radius=1
    g207: BSplineCurve PolesCount=3 KnotsCount=2 Degree=2 IsPeriodic=0
    g208: GeomPoint X=306.073 Y=73.3346 Z=0
    g209: GeomPoint X=302.567 Y=75.4095 Z=0
    g210: LineSegment StartX=302.567 StartY=-42.9683 StartZ=0 EndX=198.275 EndY=14.2954 EndZ=0
    g211: LineSegment StartX=198.275 StartY=18.1458 StartZ=0 EndX=302.567 EndY=75.4095 EndZ=0
    g212: LineSegment StartX=306.073 StartY=73.3346 StartZ=0 EndX=306.073 EndY=-40.8935 EndZ=0
    g213: LineSegment StartX=322.073 StartY=105.865 StartZ=0 EndX=328.643 EndY=105.865 EndZ=0
    g214: LineSegment StartX=318.073 StartY=120.221 StartZ=0 EndX=318.073 EndY=109.865 EndZ=0
    g215: LineSegment StartX=336.157 StartY=107.779 StartZ=0 EndX=362.567 EndY=122.294 EndZ=0
    g216: Circle CenterX=362.073 CenterY=124.221 CenterZ=0 NormalX=0 NormalY=0 NormalZ=1 AngleXU=0 Radius=1
    g217: Circle CenterX=366.073 CenterY=124.221 CenterZ=0 NormalX=0 NormalY=0 NormalZ=1 AngleXU=0 Radius=1
    g218: Circle CenterX=362.567 CenterY=122.294 CenterZ=0 NormalX=0 NormalY=0 NormalZ=1 AngleXU=0 Radius=1
    g219: BSplineCurve PolesCount=3 KnotsCount=2 Degree=2 IsPeriodic=0
    g220: GeomPoint X=362.073 Y=124.221 Z=0
    g221: GeomPoint X=362.567 Y=122.294 Z=0
    g222: Circle CenterX=322.073 CenterY=124.221 CenterZ=0 NormalX=0 NormalY=0 NormalZ=1 AngleXU=0 Radius=1
    g223: Circle CenterX=318.073 CenterY=124.221 CenterZ=0 NormalX=0 NormalY=0 NormalZ=1 AngleXU=0 Radius=1
    g224: Circle CenterX=318.073 CenterY=120.221 CenterZ=0 NormalX=0 NormalY=0 NormalZ=1 AngleXU=0 Radius=1
    g225: BSplineCurve PolesCount=3 KnotsCount=2 Degree=2 IsPeriodic=0
    g226: GeomPoint X=322.073 Y=124.221 Z=0
    g227: GeomPoint X=318.073 Y=120.221 Z=0
    g228: Circle CenterX=322.073 CenterY=105.865 CenterZ=0 NormalX=0 NormalY=0 NormalZ=1 AngleXU=0 Radius=1
    g229: Circle CenterX=318.073 CenterY=105.865 CenterZ=0 NormalX=0 NormalY=0 NormalZ=1 AngleXU=0 Radius=1
    g230: Circle CenterX=318.073 CenterY=109.865 CenterZ=0 NormalX=0 NormalY=0 NormalZ=1 AngleXU=0 Radius=1
    g231: BSplineCurve PolesCount=3 KnotsCount=2 Degree=2 IsPeriodic=0
    g232: GeomPoint X=322.073 Y=105.865 Z=0
    g233: GeomPoint X=318.073 Y=109.865 Z=0
    g234: Circle CenterX=336.157 CenterY=107.779 CenterZ=0 NormalX=0 NormalY=0 NormalZ=1 AngleXU=0 Radius=1
    g235: Circle CenterX=332.651 CenterY=105.853 CenterZ=0 NormalX=0 NormalY=0 NormalZ=1 AngleXU=0 Radius=1
    g236: Circle CenterX=328.643 CenterY=105.865 CenterZ=0 NormalX=0 NormalY=0 NormalZ=1 AngleXU=0 Radius=1
    g237: BSplineCurve PolesCount=3 KnotsCount=2 Degree=2 IsPeriodic=0
    g238: GeomPoint X=336.157 Y=107.779 Z=0
    g239: GeomPoint X=328.643 Y=105.865 Z=0
    g240: LineSegment StartX=322.073 StartY=124.221 StartZ=0 EndX=362.073 EndY=124.221 EndZ=0
    g241: Circle CenterX=371.567 CenterY=-80.8644 CenterZ=0 NormalX=0 NormalY=0 NormalZ=1 AngleXU=0 Radius=1
    g242: Circle CenterX=375.073 CenterY=-82.7896 CenterZ=0 NormalX=0 NormalY=0 NormalZ=1 AngleXU=0 Radius=1
    g243: Circle CenterX=375.073 CenterY=-78.7896 CenterZ=0 NormalX=0 NormalY=0 NormalZ=1 AngleXU=0 Radius=1
    g244: BSplineCurve PolesCount=3 KnotsCount=2 Degree=2 IsPeriodic=0
    g245: GeomPoint X=371.567 Y=-80.8644 Z=0
    g246: GeomPoint X=375.073 Y=-78.7896 Z=0
    g247: Circle CenterX=321.579 CenterY=-53.4075 CenterZ=0 NormalX=0 NormalY=0 NormalZ=1 AngleXU=0 Radius=1
    g248: Circle CenterX=318.073 CenterY=-51.4823 CenterZ=0 NormalX=0 NormalY=0 NormalZ=1 AngleXU=0 Radius=1
    g249: Circle CenterX=318.073 CenterY=-47.4805 CenterZ=0 NormalX=0 NormalY=0 NormalZ=1 AngleXU=0 Radius=1
    g250: BSplineCurve PolesCount=3 KnotsCount=2 Degree=2 IsPeriodic=0
    g251: GeomPoint X=321.579 Y=-53.4075 Z=0
    g252: GeomPoint X=318.073 Y=-47.4805 Z=0
    g253: LineSegment StartX=371.567 StartY=-80.8644 StartZ=0 EndX=321.579 EndY=-53.4075 EndZ=0
    g254: Circle CenterX=321.579 CenterY=-67.3492 CenterZ=0 NormalX=0 NormalY=0 NormalZ=1 AngleXU=0 Radius=1
    g255: Circle CenterX=318.073 CenterY=-65.424 CenterZ=0 NormalX=0 NormalY=0 NormalZ=1 AngleXU=0 Radius=1
    g256: Circle CenterX=318.073 CenterY=-69.424 CenterZ=0 NormalX=0 NormalY=0 NormalZ=1 AngleXU=0 Radius=1
    g257: BSplineCurve PolesCount=3 KnotsCount=2 Degree=2 IsPeriodic=0
    g258: GeomPoint X=321.579 Y=-67.3492 Z=0
    g259: GeomPoint X=318.073 Y=-69.424 Z=0
    g260: Circle CenterX=362.567 CenterY=-89.8542 CenterZ=0 NormalX=0 NormalY=0 NormalZ=1 AngleXU=0 Radius=1
    g261: Circle CenterX=366.073 CenterY=-91.7794 CenterZ=0 NormalX=0 NormalY=0 NormalZ=1 AngleXU=0 Radius=1
    g262: Circle CenterX=362.073 CenterY=-91.7794 CenterZ=0 NormalX=0 NormalY=0 NormalZ=1 AngleXU=0 Radius=1
    g263: BSplineCurve PolesCount=3 KnotsCount=2 Degree=2 IsPeriodic=0
    g264: GeomPoint X=362.567 Y=-89.8542 Z=0
    g265: GeomPoint X=362.073 Y=-91.7794 Z=0
    g266: Circle CenterX=322.073 CenterY=-91.7794 CenterZ=0 NormalX=0 NormalY=0 NormalZ=1 AngleXU=0 Radius=1
    g267: Circle CenterX=318.073 CenterY=-91.7794 CenterZ=0 NormalX=0 NormalY=0 NormalZ=1 AngleXU=0 Radius=1
    g268: Circle CenterX=318.073 CenterY=-87.7794 CenterZ=0 NormalX=0 NormalY=0 NormalZ=1 AngleXU=0 Radius=1
    g269: BSplineCurve PolesCount=3 KnotsCount=2 Degree=2 IsPeriodic=0
    g270: GeomPoint X=322.073 Y=-91.7794 Z=0
    g271: GeomPoint X=318.073 Y=-87.7794 Z=0
    g272: LineSegment StartX=362.567 StartY=-89.8542 StartZ=0 EndX=321.579 EndY=-67.3492 EndZ=0
    g273: LineSegment StartX=318.073 StartY=-69.424 StartZ=0 EndX=318.073 EndY=-87.7794 EndZ=0
    g274: LineSegment StartX=322.073 StartY=-91.7794 StartZ=0 EndX=362.073 EndY=-91.7794 EndZ=0
    g275: Circle CenterX=2.07281 CenterY=124.221 CenterZ=0 NormalX=0 NormalY=0 NormalZ=1 AngleXU=0 Radius=1
    g276: Circle CenterX=1.57905 CenterY=122.295 CenterZ=0 NormalX=0 NormalY=0 NormalZ=1 AngleXU=0 Radius=1
    g277: BSplineCurve PolesCount=3 KnotsCount=2 Degree=2 IsPeriodic=0
    g278: GeomPoint X=2.07281 Y=124.221 Z=0
    g279: GeomPoint X=1.57905 Y=122.295 Z=0
    g280: Circle CenterX=42.0728 CenterY=124.221 CenterZ=0 NormalX=0 NormalY=0 NormalZ=1 AngleXU=0 Radius=1
    g281: Circle CenterX=46.0728 CenterY=124.221 CenterZ=0 NormalX=0 NormalY=0 NormalZ=1 AngleXU=0 Radius=1
    g282: Circle CenterX=46.0728 CenterY=120.221 CenterZ=0 NormalX=0 NormalY=0 NormalZ=1 AngleXU=0 Radius=1
    g283: BSplineCurve PolesCount=3 KnotsCount=2 Degree=2 IsPeriodic=0
    g284: GeomPoint X=42.0728 Y=124.221 Z=0
    g285: GeomPoint X=46.0728 Y=120.221 Z=0
    g286: Circle CenterX=46.0728 CenterY=109.865 CenterZ=0 NormalX=0 NormalY=0 NormalZ=1 AngleXU=0 Radius=1
    g287: Circle CenterX=46.0728 CenterY=105.865 CenterZ=0 NormalX=0 NormalY=0 NormalZ=1 AngleXU=0 Radius=1
    g288: Circle CenterX=42.0728 CenterY=105.865 CenterZ=0 NormalX=0 NormalY=0 NormalZ=1 AngleXU=0 Radius=1
    g289: BSplineCurve PolesCount=3 KnotsCount=2 Degree=2 IsPeriodic=0
    g290: GeomPoint X=46.0728 Y=109.865 Z=0
    g291: GeomPoint X=42.0728 Y=105.865 Z=0
    g292: Circle CenterX=35.5028 CenterY=105.865 CenterZ=0 NormalX=0 NormalY=0 NormalZ=1 AngleXU=0 Radius=1
    g293: Circle CenterX=31.5028 CenterY=105.865 CenterZ=0 NormalX=0 NormalY=0 NormalZ=1 AngleXU=0 Radius=1
    g294: Circle CenterX=27.9965 CenterY=107.79 CenterZ=0 NormalX=0 NormalY=0 NormalZ=1 AngleXU=0 Radius=1
    g295: BSplineCurve PolesCount=3 KnotsCount=2 Degree=2 IsPeriodic=0
    g296: GeomPoint X=35.5028 Y=105.865 Z=0
    g297: GeomPoint X=27.9965 Y=107.79 Z=0
    g298: LineSegment StartX=2.07281 StartY=124.221 StartZ=0 EndX=42.0728 EndY=124.221 EndZ=0
    g299: LineSegment StartX=46.0728 StartY=120.221 StartZ=0 EndX=46.0728 EndY=109.865 EndZ=0
    g300: LineSegment StartX=42.0728 StartY=105.865 StartZ=0 EndX=35.5028 EndY=105.865 EndZ=0
    g301: LineSegment StartX=27.9965 StartY=107.79 StartZ=0 EndX=1.57905 EndY=122.295 EndZ=0
    g302: Circle CenterX=42.5666 CenterY=-67.3492 CenterZ=0 NormalX=0 NormalY=0 NormalZ=1 AngleXU=0 Radius=1
    g303: Circle CenterX=46.0728 CenterY=-65.424 CenterZ=0 NormalX=0 NormalY=0 NormalZ=1 AngleXU=0 Radius=1
    g304: Circle CenterX=46.0728 CenterY=-69.424 CenterZ=0 NormalX=0 NormalY=0 NormalZ=1 AngleXU=0 Radius=1
    g305: BSplineCurve PolesCount=3 KnotsCount=2 Degree=2 IsPeriodic=0
    g306: GeomPoint X=42.5666 Y=-67.3492 Z=0
    g307: GeomPoint X=46.0728 Y=-69.424 Z=0
    g308: Circle CenterX=46.0728 CenterY=-87.7794 CenterZ=0 NormalX=0 NormalY=0 NormalZ=1 AngleXU=0 Radius=1
    g309: Circle CenterX=46.0728 CenterY=-91.7794 CenterZ=0 NormalX=0 NormalY=0 NormalZ=1 AngleXU=0 Radius=1
    g310: Circle CenterX=42.0728 CenterY=-91.7794 CenterZ=0 NormalX=0 NormalY=0 NormalZ=1 AngleXU=0 Radius=1
    g311: BSplineCurve PolesCount=3 KnotsCount=2 Degree=2 IsPeriodic=0
    g312: GeomPoint X=46.0728 Y=-87.7794 Z=0
    g313: GeomPoint X=42.0728 Y=-91.7794 Z=0
    g314: Circle CenterX=2.07281 CenterY=-91.7794 CenterZ=0 NormalX=0 NormalY=0 NormalZ=1 AngleXU=0 Radius=1
    g315: Circle CenterX=-1.92719 CenterY=-91.7794 CenterZ=0 NormalX=0 NormalY=0 NormalZ=1 AngleXU=0 Radius=1
    g316: Circle CenterX=1.57905 CenterY=-89.8542 CenterZ=0 NormalX=0 NormalY=0 NormalZ=1 AngleXU=0 Radius=1
    g317: BSplineCurve PolesCount=3 KnotsCount=2 Degree=2 IsPeriodic=0
    g318: GeomPoint X=2.07281 Y=-91.7794 Z=0
    g319: GeomPoint X=1.57905 Y=-89.8542 Z=0
    g320: LineSegment StartX=2.07281 StartY=-91.7794 StartZ=0 EndX=42.0728 EndY=-91.7794 EndZ=0
    g321: LineSegment StartX=46.0728 StartY=-87.7794 StartZ=0 EndX=46.0728 EndY=-69.424 EndZ=0
    g322: LineSegment StartX=42.5666 StartY=-67.3492 StartZ=0 EndX=1.57905 EndY=-89.8542 EndZ=0
    g323: Circle CenterX=322.073 CenterY=76.4095 CenterZ=0 NormalX=0 NormalY=0 NormalZ=1 AngleXU=0 Radius=4
    g324: BSplineCurve PolesCount=3 KnotsCount=2 Degree=2 IsPeriodic=0
    g325: GeomPoint X=318.073 Y=72.4095 Z=0
    g326: GeomPoint X=322.073 Y=76.4095 Z=0
    g327: Circle CenterX=375.073 CenterY=72.4095 CenterZ=0 NormalX=0 NormalY=0 NormalZ=1 AngleXU=0 Radius=1
    g328: Circle CenterX=375.073 CenterY=76.4095 CenterZ=0 NormalX=0 NormalY=0 NormalZ=1 AngleXU=0 Radius=1
    g329: Circle CenterX=371.073 CenterY=76.4095 CenterZ=0 NormalX=0 NormalY=0 NormalZ=1 AngleXU=0 Radius=1
    g330: BSplineCurve PolesCount=3 KnotsCount=2 Degree=2 IsPeriodic=0
    g331: GeomPoint X=375.073 Y=72.4095 Z=0
    g332: GeomPoint X=371.073 Y=76.4095 Z=0
    g333: LineSegment StartX=322.073 StartY=76.4095 StartZ=0 EndX=371.073 EndY=76.4095 EndZ=0
    g334: LineSegment StartX=318.073 StartY=72.4095 StartZ=0 EndX=318.073 EndY=-47.4805 EndZ=0
    g335: LineSegment StartX=375.073 StartY=72.4095 StartZ=0 EndX=375.073 EndY=-78.7896 EndZ=0
    g336: ArcOfCircle CenterX=-26.9272 CenterY=22.1087 CenterZ=0 NormalX=0 NormalY=0 NormalZ=1 AngleXU=0 Radius=4 StartAngle=5e-16 EndAngle=3.14159
    g337: LineSegment StartX=-22.9272 StartY=22.1087 StartZ=0 EndX=-18.9272 EndY=-83.7794 EndZ=0
    g338: LineSegment StartX=-34.9272 StartY=-83.7794 StartZ=0 EndX=-30.9272 EndY=22.1087 EndZ=0
    g339: ArcOfCircle CenterX=391.073 CenterY=22.1087 CenterZ=0 NormalX=0 NormalY=0 NormalZ=1 AngleXU=0 Radius=4 StartAngle=0 EndAngle=3.14159
    g340: LineSegment StartX=387.073 StartY=22.1087 StartZ=0 EndX=383.073 EndY=-83.7794 EndZ=0
    g341: LineSegment StartX=395.073 StartY=22.1087 StartZ=0 EndX=399.073 EndY=-83.7794 EndZ=0
    g342: Circle CenterX=-10.9272 CenterY=-78.7794 CenterZ=0 NormalX=0 NormalY=0 NormalZ=1 AngleXU=0 Radius=1
    g343: Circle CenterX=-10.9272 CenterY=-82.7794 CenterZ=0 NormalX=0 NormalY=0 NormalZ=1 AngleXU=0 Radius=1
    g344: Circle CenterX=-7.42095 CenterY=-80.8542 CenterZ=0 NormalX=0 NormalY=0 NormalZ=1 AngleXU=0 Radius=1
    g345: BSplineCurve PolesCount=3 KnotsCount=2 Degree=2 IsPeriodic=0
    g346: GeomPoint X=-10.9272 Y=-78.7794 Z=0
    g347: GeomPoint X=-7.42095 Y=-80.8542 Z=0
    g348: Circle CenterX=42.5666 CenterY=-53.4075 CenterZ=0 NormalX=0 NormalY=0 NormalZ=1 AngleXU=0 Radius=1
    g349: Circle CenterX=46.0728 CenterY=-51.4823 CenterZ=0 NormalX=0 NormalY=0 NormalZ=1 AngleXU=0 Radius=1
    g350: Circle CenterX=46.0728 CenterY=-47.4823 CenterZ=0 NormalX=0 NormalY=0 NormalZ=1 AngleXU=0 Radius=1
    g351: BSplineCurve PolesCount=3 KnotsCount=2 Degree=2 IsPeriodic=0
    g352: GeomPoint X=42.5666 Y=-53.4075 Z=0
    g353: GeomPoint X=46.0728 Y=-47.4823 Z=0
    g354: Circle CenterX=46.0728 CenterY=72.4095 CenterZ=0 NormalX=0 NormalY=0 NormalZ=1 AngleXU=0 Radius=1
    g355: Circle CenterX=46.0728 CenterY=76.4095 CenterZ=0 NormalX=0 NormalY=0 NormalZ=1 AngleXU=0 Radius=1
    g356: Circle CenterX=42.0728 CenterY=76.4095 CenterZ=0 NormalX=0 NormalY=0 NormalZ=1 AngleXU=0 Radius=1
    g357: BSplineCurve PolesCount=3 KnotsCount=2 Degree=2 IsPeriodic=0
    g358: GeomPoint X=46.0728 Y=72.4095 Z=0
    g359: GeomPoint X=42.0728 Y=76.4095 Z=0
    g360: Circle CenterX=-6.92718 CenterY=76.4095 CenterZ=0 NormalX=0 NormalY=0 NormalZ=1 AngleXU=0 Radius=1
    g361: Circle CenterX=-10.9272 CenterY=76.4095 CenterZ=0 NormalX=0 NormalY=0 NormalZ=1 AngleXU=0 Radius=1
    g362: Circle CenterX=-10.9272 CenterY=72.4095 CenterZ=0 NormalX=0 NormalY=0 NormalZ=1 AngleXU=0 Radius=1
    g363: BSplineCurve PolesCount=3 KnotsCount=2 Degree=2 IsPeriodic=0
    g364: GeomPoint X=-6.92718 Y=76.4095 Z=0
    g365: GeomPoint X=-10.9272 Y=72.4095 Z=0
    g366: LineSegment StartX=-10.9272 StartY=72.4095 StartZ=0 EndX=-10.9272 EndY=-78.7794 EndZ=0
    g367: LineSegment StartX=-7.42095 StartY=-80.8542 StartZ=0 EndX=42.5666 EndY=-53.4075 EndZ=0
    g368: LineSegment StartX=46.0728 StartY=-47.4823 StartZ=0 EndX=46.0728 EndY=72.4095 EndZ=0
    g369: LineSegment StartX=42.0728 StartY=76.4095 StartZ=0 EndX=-6.92719 EndY=76.4095 EndZ=0
    g370: LineSegment StartX=232.072 StartY=136.221 StartZ=0 EndX=232.072 EndY=-117.815 EndZ=0
    g371: LineSegment StartX=245.072 StartY=136.221 StartZ=0 EndX=245.072 EndY=-116.499 EndZ=0
    g372: LineSegment StartX=119.072 StartY=136.221 StartZ=0 EndX=119.072 EndY=-116.228 EndZ=0
    g373: LineSegment StartX=-42.9272 StartY=136.221 StartZ=0 EndX=407.073 EndY=136.221 EndZ=0
    g374: LineSegment StartX=232.072 StartY=136.221 StartZ=0 EndX=220.072 EndY=136.221 EndZ=0
    g375: LineSegment StartX=232.072 StartY=136.221 StartZ=0 EndX=232.072 EndY=124.221 EndZ=0
    g376: LineSegment StartX=220.072 StartY=136.221 StartZ=0 EndX=220.072 EndY=124.221 EndZ=0
    g377: LineSegment StartX=220.072 StartY=136.221 StartZ=0 EndX=226.072 EndY=136.221 EndZ=0
    g378: LineSegment StartX=220.072 StartY=136.221 StartZ=0 EndX=220.072 EndY=130.221 EndZ=0
    g379: LineSegment StartX=220.072 StartY=124.221 StartZ=0 EndX=226.072 EndY=124.221 EndZ=0
    g380: LineSegment StartX=232.072 StartY=124.221 StartZ=0 EndX=232.072 EndY=127.221 EndZ=0
    g381: LineSegment StartX=232.072 StartY=136.221 StartZ=0 EndX=232.072 EndY=133.221 EndZ=0
    g382-g386: Circle x5 (B-spline internal-alignment scaffolding for g387; pole/knot coordinates omitted)
    g387: BSplineCurve PolesCount=5 KnotsCount=3 Degree=3 IsPeriodic=0
    g388: GeomPoint X=232.072 Y=133.221 Z=0
    g389: GeomPoint X=223.072 Y=130.221 Z=0
    g390: GeomPoint X=232.072 Y=127.221 Z=0
    g391: LineSegment StartX=189.124 StartY=124.221 StartZ=0 EndX=302.073 EndY=124.221 EndZ=0
    g392: LineSegment StartX=132.072 StartY=136.221 StartZ=0 EndX=132.072 EndY=124.221 EndZ=0
    g393: LineSegment StartX=132.072 StartY=136.221 StartZ=0 EndX=144.072 EndY=136.221 EndZ=0
    g394: LineSegment StartX=144.072 StartY=136.221 StartZ=0 EndX=144.072 EndY=124.221 EndZ=0
    g395: LineSegment StartX=144.072 StartY=136.221 StartZ=0 EndX=138.072 EndY=136.221 EndZ=0
    g396: LineSegment StartX=144.072 StartY=136.221 StartZ=0 EndX=144.072 EndY=130.221 EndZ=0
    g397: LineSegment StartX=132.072 StartY=136.221 StartZ=0 EndX=132.072 EndY=133.221 EndZ=0
    g398: LineSegment StartX=132.072 StartY=133.221 StartZ=0 EndX=132.072 EndY=127.221 EndZ=0
    g399-g403: Circle x5 (B-spline internal-alignment scaffolding for g404; pole/knot coordinates omitted)
    g404: BSplineCurve PolesCount=5 KnotsCount=3 Degree=3 IsPeriodic=0
    g405: GeomPoint X=132.072 Y=133.221 Z=0
    g406: GeomPoint X=141.072 Y=130.221 Z=0
    g407: GeomPoint X=132.072 Y=127.221 Z=0
    ... +7 more geometry lines
  constraints (702):
    c: Vertical(g0)
    c: Vertical(g1)
    c: Block(g1)
    c: Block(g0)
    c: Weight(g4) = 1
    c: Equal(g4,g5)
    c: Equal(g4,g6)
    c: InternalAlignment(g4,g7)
    c: InternalAlignment(g5,g7)
    c: InternalAlignment(g6,g7)
    c: InternalAlignment(g8,g7)
    c: InternalAlignment(g9,g7)
    c: Weight(g10) = 1
    c: Equal(g10,g11)
    c: Equal(g10,g12)
    c: InternalAlignment(g10,g13)
    c: InternalAlignment(g11,g13)
    c: InternalAlignment(g12,g13)
    c: InternalAlignment(g14,g13)
    c: InternalAlignment(g15,g13)
    c: Block(g13)
    c: Block(g7)
    c: Weight(g16) = 1
    c: Equal(g16,g17)
    c: Equal(g16,g18)
    c: InternalAlignment(g16,g19)
    c: InternalAlignment(g17,g19)
    c: InternalAlignment(g18,g19)
    c: InternalAlignment(g20,g19)
    c: InternalAlignment(g21,g19)
    c: Weight(g22) = 1
    c: Equal(g22,g23)
    c: Equal(g22,g24)
    c: InternalAlignment(g22,g25)
    c: InternalAlignment(g23,g25)
    c: InternalAlignment(g24,g25)
    c: InternalAlignment(g26,g25)
    c: InternalAlignment(g27,g25)
    c: Block(g25)
    c: Block(g19)
    c: Weight(g28) = 1
    c: Equal(g28,g29)
    c: Equal(g28,g30)
    c: InternalAlignment(g28,g31)
    c: InternalAlignment(g29,g31)
    c: InternalAlignment(g30,g31)
    c: InternalAlignment(g32,g31)
    c: InternalAlignment(g33,g31)
    c: Weight(g34) = 1
    c: Equal(g34,g35)
    c: Equal(g34,g36)
    c: InternalAlignment(g34,g37)
    c: InternalAlignment(g35,g37)
    c: InternalAlignment(g36,g37)
    c: InternalAlignment(g38,g37)
    c: InternalAlignment(g39,g37)
    c: Block(g31)
    c: Block(g37)
    c: Coincident(g40,g1)
    c: Coincident(g40,g0)
    c: Horizontal(g40)
    c: Distance(g40) = 450
    c: Weight(g41) = 1
    c: Equal(g41,g42)
    c: Equal(g41,g43)
    c: InternalAlignment(g41,g44)
    c: InternalAlignment(g42,g44)
    c: InternalAlignment(g43,g44)
    c: InternalAlignment(g45,g44)
    c: InternalAlignment(g46,g44)
    c: Block(g44)
    c: Weight(g47) = 1
    c: Equal(g47,g48)
    c: Equal(g47,g49)
    c: InternalAlignment(g47,g50)
    c: InternalAlignment(g48,g50)
    c: InternalAlignment(g49,g50)
    c: InternalAlignment(g51,g50)
    c: InternalAlignment(g52,g50)
    c: Block(g50)
    c: Weight(g53) = 1
    c: Equal(g53,g54)
    c: Equal(g53,g55)
    c: InternalAlignment(g53,g56)
    c: InternalAlignment(g54,g56)
    c: InternalAlignment(g55,g56)
    c: InternalAlignment(g57,g56)
    c: InternalAlignment(g58,g56)
    c: Block(g56)
    c: Weight(g59) = 1
    c: Equal(g59,g60)
    c: Equal(g59,g61)
    c: InternalAlignment(g59,g62)
    c: InternalAlignment(g60,g62)
    c: InternalAlignment(g61,g62)
    c: InternalAlignment(g63,g62)
    c: InternalAlignment(g64,g62)
    c: Block(g62)
    c: Weight(g65) = 1
    c: Equal(g65,g66)
    c: Equal(g65,g67)
    c: InternalAlignment(g65,g68)
    c: InternalAlignment(g66,g68)
    c: InternalAlignment(g67,g68)
    c: InternalAlignment(g69,g68)
    c: InternalAlignment(g70,g68)
    c: Weight(g71) = 1
    c: Equal(g71,g72)
    c: Equal(g71,g73)
    c: InternalAlignment(g71,g74)
    c: InternalAlignment(g72,g74)
    c: InternalAlignment(g73,g74)
    c: InternalAlignment(g75,g74)
    c: InternalAlignment(g76,g74)
    c: Block(g68)
    c: Block(g74)
    c: Coincident(g77,g68)
    c: Coincident(g77,g74)
    c: Vertical(g77)
    c: Coincident(g78,g68)
    c: Coincident(g78,g50)
    c: Coincident(g79,g50)
    c: Coincident(g79,g74)
    c: Weight(g80) = 1
    c: Equal(g80,g81)
    c: Equal(g80,g82)
    c: InternalAlignment(g80,g83)
    c: InternalAlignment(g81,g83)
    c: InternalAlignment(g82,g83)
    c: InternalAlignment(g84,g83)
    c: InternalAlignment(g85,g83)
    c: Weight(g86) = 1
    c: Equal(g86,g87)
    c: Equal(g86,g88)
    c: InternalAlignment(g86,g89)
    c: InternalAlignment(g87,g89)
    c: InternalAlignment(g88,g89)
    c: InternalAlignment(g90,g89)
    c: InternalAlignment(g91,g89)
    c: Block(g83)
    c: Block(g89)
    c: Coincident(g92,g83)
    c: Coincident(g92,g89)
    c: Vertical(g92)
    c: Coincident(g93,g83)
    c: Coincident(g93,g44)
    c: Coincident(g94,g44)
    c: Coincident(g94,g89)
    c: Weight(g95) = 1
    c: Equal(g95,g96)
    c: Equal(g95,g97)
    c: InternalAlignment(g95,g98)
    c: InternalAlignment(g96,g98)
    c: InternalAlignment(g97,g98)
    c: InternalAlignment(g99,g98)
    c: InternalAlignment(g100,g98)
    c: Weight(g101) = 1
    c: Equal(g101,g102)
    c: Equal(g101,g103)
    c: InternalAlignment(g101,g104)
    c: InternalAlignment(g102,g104)
    c: InternalAlignment(g103,g104)
    c: InternalAlignment(g105,g104)
    c: InternalAlignment(g106,g104)
    c: Block(g98)
    c: Block(g104)
    c: Coincident(g107,g98)
    c: Coincident(g107,g104)
    c: Vertical(g107)
    c: Coincident(g108,g104)
    c: Coincident(g108,g62)
    c: Coincident(g109,g62)
    c: Coincident(g109,g98)
    c: Weight(g110) = 1
    c: Equal(g110,g111)
    c: Equal(g110,g112)
    c: InternalAlignment(g110,g113)
    c: InternalAlignment(g111,g113)
    c: InternalAlignment(g112,g113)
    c: InternalAlignment(g114,g113)
    c: InternalAlignment(g115,g113)
    c: Weight(g116) = 1
    c: Equal(g116,g117)
    c: Equal(g116,g118)
    c: InternalAlignment(g116,g119)
    c: InternalAlignment(g117,g119)
    c: InternalAlignment(g118,g119)
    c: InternalAlignment(g120,g119)
    c: InternalAlignment(g121,g119)
    c: Block(g113)
    c: Block(g119)
    c: Coincident(g122,g113)
    c: Coincident(g122,g119)
    c: Vertical(g122)
    c: Coincident(g123,g119)
    c: Coincident(g123,g56)
    c: Coincident(g124,g56)
    c: Coincident(g124,g113)
    c: Weight(g125) = 1
    c: Equal(g125,g126)
    c: Equal(g125,g127)
    c: InternalAlignment(g125,g128)
    c: InternalAlignment(g126,g128)
    c: InternalAlignment(g127,g128)
    c: InternalAlignment(g129,g128)
    c: InternalAlignment(g130,g128)
    c: Weight(g131) = 1
    c: Equal(g131,g132)
    c: Equal(g131,g133)
    c: InternalAlignment(g131,g134)
    c: InternalAlignment(g132,g134)
    c: InternalAlignment(g133,g134)
    c: InternalAlignment(g135,g134)
    c: InternalAlignment(g136,g134)
    c: Weight(g137) = 1
    c: Equal(g137,g138)
    c: Equal(g137,g139)
    c: InternalAlignment(g137,g140)
    c: InternalAlignment(g138,g140)
    c: InternalAlignment(g139,g140)
    c: InternalAlignment(g141,g140)
    c: InternalAlignment(g142,g140)
    c: Weight(g143) = 1
    c: Equal(g143,g144)
    c: Equal(g143,g145)
    c: InternalAlignment(g143,g146)
    c: InternalAlignment(g144,g146)
    c: InternalAlignment(g145,g146)
    c: InternalAlignment(g147,g146)
    c: InternalAlignment(g148,g146)
    c: Block(g146)
    c: Block(g140)
    c: Block(g134)
    c: Block(g128)
    c: Coincident(g149,g25)
    c: Coincident(g149,g146)
    c: Coincident(g150,g146)
    c: Coincident(g150,g140)
    c: Horizontal(g150)
    c: Coincident(g151,g140)
    c: Coincident(g151,g25)
    c: Vertical(g151)
    c: Coincident(g152,g19)
    c: Coincident(g152,g134)
    c: Vertical(g152)
    c: Coincident(g153,g134)
    c: Coincident(g153,g128)
    c: Horizontal(g153)
    c: Coincident(g154,g128)
    c: Coincident(g154,g19)
    c: Weight(g155) = 1
    c: Equal(g155,g156)
    c: Equal(g155,g157)
    c: InternalAlignment(g155,g158)
    c: InternalAlignment(g156,g158)
    c: InternalAlignment(g157,g158)
    c: InternalAlignment(g159,g158)
    c: InternalAlignment(g160,g158)
    c: Weight(g161) = 1
    c: Equal(g161,g162)
    c: Equal(g161,g163)
    c: InternalAlignment(g161,g164)
    c: InternalAlignment(g162,g164)
    c: InternalAlignment(g163,g164)
    c: InternalAlignment(g165,g164)
    c: InternalAlignment(g166,g164)
    c: Weight(g167) = 1
    c: Equal(g167,g168)
    c: Equal(g167,g169)
    c: InternalAlignment(g167,g170)
    c: InternalAlignment(g168,g170)
    c: InternalAlignment(g169,g170)
    c: InternalAlignment(g171,g170)
    c: InternalAlignment(g172,g170)
    c: Weight(g173) = 1
    c: Equal(g173,g174)
    c: Equal(g173,g175)
    c: InternalAlignment(g173,g176)
    c: InternalAlignment(g174,g176)
    c: InternalAlignment(g175,g176)
    c: InternalAlignment(g177,g176)
    c: InternalAlignment(g178,g176)
    c: Block(g176)
    c: Block(g170)
    c: Block(g164)
    c: Block(g158)
    c: Coincident(g179,g170)
    c: Coincident(g179,g7)
    c: Vertical(g179)
    c: Coincident(g180,g13)
    c: Coincident(g180,g164)
    c: Vertical(g180)
    c: Coincident(g181,g158)
    c: Coincident(g181,g13)
    c: Coincident(g182,g7)
    c: Weight(g183) = 1
    c: Equal(g183,g184)
    c: Equal(g183,g185)
    c: InternalAlignment(g183,g186)
    c: InternalAlignment(g184,g186)
    c: InternalAlignment(g185,g186)
    c: InternalAlignment(g187,g186)
    c: InternalAlignment(g188,g186)
    c: Weight(g189) = 1
    c: Equal(g189,g190)
    c: Equal(g189,g191)
    c: InternalAlignment(g189,g192)
    c: InternalAlignment(g190,g192)
    c: InternalAlignment(g191,g192)
    c: InternalAlignment(g193,g192)
    c: InternalAlignment(g194,g192)
    c: Block(g192)
    c: Block(g186)
    c: Coincident(g195,g192)
    c: Coincident(g195,g31)
    c: Coincident(g196,g31)
    c: Coincident(g196,g186)
    c: Coincident(g197,g186)
    c: Coincident(g197,g192)
    c: Vertical(g197)
    c: Weight(g198) = 1
    c: Equal(g198,g199)
    c: Equal(g198,g200)
    c: InternalAlignment(g198,g201)
    c: InternalAlignment(g199,g201)
    c: InternalAlignment(g200,g201)
    c: InternalAlignment(g202,g201)
    c: InternalAlignment(g203,g201)
    c: Weight(g204) = 1
    c: Equal(g204,g205)
    c: Equal(g204,g206)
    c: InternalAlignment(g204,g207)
    c: InternalAlignment(g205,g207)
    c: InternalAlignment(g206,g207)
    c: InternalAlignment(g208,g207)
    c: InternalAlignment(g209,g207)
    c: Block(g207)
    c: Block(g201)
    c: Coincident(g210,g201)
    c: Coincident(g210,g37)
    c: Coincident(g211,g37)
    c: Coincident(g211,g207)
    c: Coincident(g212,g207)
    c: Coincident(g212,g201)
    c: Vertical(g212)
    c: Horizontal(g213)
    c: Block(g213)
    c: Vertical(g214)
    c: Block(g214)
    c: Block(g215)
    c: Weight(g216) = 1
    c: Equal(g216,g217)
    c: Equal(g216,g218)
    c: InternalAlignment(g216,g219)
    c: InternalAlignment(g217,g219)
    c: InternalAlignment(g218,g219)
    c: InternalAlignment(g220,g219)
    c: InternalAlignment(g221,g219)
    c: Weight(g222) = 1
    c: Equal(g222,g223)
    c: Equal(g222,g224)
    c: InternalAlignment(g222,g225)
    c: InternalAlignment(g223,g225)
    c: InternalAlignment(g224,g225)
    c: InternalAlignment(g226,g225)
    c: InternalAlignment(g227,g225)
    c: Weight(g228) = 1
    c: Equal(g228,g229)
    c: Equal(g228,g230)
    c: InternalAlignment(g228,g231)
    c: InternalAlignment(g229,g231)
    c: InternalAlignment(g230,g231)
    c: InternalAlignment(g232,g231)
    c: InternalAlignment(g233,g231)
    c: Weight(g234) = 1
    c: Equal(g234,g235)
    c: Equal(g234,g236)
    c: InternalAlignment(g234,g237)
    c: InternalAlignment(g235,g237)
    c: InternalAlignment(g236,g237)
    c: InternalAlignment(g238,g237)
    c: InternalAlignment(g239,g237)
    c: Block(g219)
    c: Block(g225)
    c: Block(g231)
    c: Block(g237)
    c: Coincident(g240,g225)
    c: Coincident(g240,g219)
    c: Horizontal(g240)
    c: Block(g182)
    c: Weight(g241) = 1
    c: Equal(g241,g242)
    c: Equal(g241,g243)
    c: InternalAlignment(g241,g244)
    c: InternalAlignment(g242,g244)
    c: InternalAlignment(g243,g244)
    c: InternalAlignment(g245,g244)
    c: InternalAlignment(g246,g244)
    c: Weight(g247) = 1
    c: Equal(g247,g248)
    c: Equal(g247,g249)
    c: InternalAlignment(g247,g250)
    c: InternalAlignment(g248,g250)
    c: InternalAlignment(g249,g250)
    c: InternalAlignment(g251,g250)
    c: InternalAlignment(g252,g250)
    c: Block(g244)
    c: Block(g250)
    c: Coincident(g253,g244)
    c: Coincident(g253,g250)
    c: Weight(g254) = 1
    c: Equal(g254,g255)
    c: Equal(g254,g256)
    c: InternalAlignment(g254,g257)
    c: InternalAlignment(g255,g257)
    c: InternalAlignment(g256,g257)
    c: InternalAlignment(g258,g257)
    c: InternalAlignment(g259,g257)
    c: Weight(g260) = 1
    c: Equal(g260,g261)
    c: Equal(g260,g262)
    c: InternalAlignment(g260,g263)
    c: InternalAlignment(g261,g263)
    c: InternalAlignment(g262,g263)
    c: InternalAlignment(g264,g263)
    c: InternalAlignment(g265,g263)
    c: Weight(g266) = 1
    c: Equal(g266,g267)
    c: Equal(g266,g268)
    c: InternalAlignment(g266,g269)
    c: InternalAlignment(g267,g269)
    c: InternalAlignment(g268,g269)
    c: InternalAlignment(g270,g269)
    c: InternalAlignment(g271,g269)
    c: Block(g269)
    c: Block(g263)
    c: Block(g257)
    c: Coincident(g272,g263)
    c: Coincident(g272,g257)
    c: Coincident(g273,g257)
    c: Coincident(g273,g269)
    c: Vertical(g273)
    c: Coincident(g274,g269)
    c: Coincident(g274,g263)
    c: Horizontal(g274)
    c: Weight(g275) = 1
    c: Equal(g275,g276)
    c: InternalAlignment(g275,g277)
    c: InternalAlignment(g276,g277)
    c: InternalAlignment(g278,g277)
    c: InternalAlignment(g279,g277)
    c: Weight(g280) = 1
    c: InternalAlignment(g281,g283)
    c: InternalAlignment(g282,g283)
    c: InternalAlignment(g284,g283)
    c: InternalAlignment(g285,g283)
    c: Weight(g286) = 1
    c: Equal(g286,g287)
    c: Equal(g286,g288)
    c: InternalAlignment(g286,g289)
    c: InternalAlignment(g287,g289)
    c: InternalAlignment(g288,g289)
    c: InternalAlignment(g290,g289)
    c: InternalAlignment(g291,g289)
    c: Equal(g292,g293)
    c: Equal(g292,g294)
    c: InternalAlignment(g292,g295)
    c: InternalAlignment(g293,g295)
    c: InternalAlignment(g294,g295)
    c: InternalAlignment(g296,g295)
    c: InternalAlignment(g297,g295)
    c: Block(g283)
    c: Block(g289)
    c: Block(g295)
    c: Block(g277)
    c: Coincident(g298,g277)
    c: Coincident(g298,g283)
    c: Horizontal(g298)
    c: Coincident(g299,g283)
    c: Coincident(g299,g289)
    c: Vertical(g299)
    c: Coincident(g300,g289)
    c: Coincident(g300,g295)
    c: Horizontal(g300)
    c: Coincident(g301,g295)
    c: Coincident(g301,g277)
    c: Weight(g302) = 1
    c: Equal(g302,g303)
    c: Equal(g302,g304)
    c: InternalAlignment(g302,g305)
    c: InternalAlignment(g303,g305)
    c: InternalAlignment(g304,g305)
    c: InternalAlignment(g306,g305)
    c: InternalAlignment(g307,g305)
    c: Weight(g308) = 1
    c: Equal(g308,g309)
    c: Equal(g308,g310)
    c: InternalAlignment(g308,g311)
    c: InternalAlignment(g309,g311)
    c: InternalAlignment(g310,g311)
    c: InternalAlignment(g312,g311)
    c: Weight(g314) = 1
    c: Equal(g314,g315)
    c: Equal(g314,g316)
    c: InternalAlignment(g314,g317)
    c: InternalAlignment(g315,g317)
    c: InternalAlignment(g316,g317)
    c: InternalAlignment(g318,g317)
    c: InternalAlignment(g319,g317)
    c: Block(g317)
    c: Block(g311)
    c: Block(g305)
    c: Coincident(g320,g317)
    c: Coincident(g320,g311)
    c: Horizontal(g320)
    c: Coincident(g321,g311)
    c: Coincident(g321,g305)
    c: Vertical(g321)
    c: Coincident(g322,g305)
    c: Coincident(g322,g317)
    c: InternalAlignment(g323,g324)
    c: InternalAlignment(g325,g324)
    c: InternalAlignment(g326,g324)
    c: Block(g324)
    c: Equal(g327,g328)
    c: Equal(g327,g329)
    c: InternalAlignment(g327,g330)
    c: InternalAlignment(g328,g330)
    c: InternalAlignment(g329,g330)
    c: InternalAlignment(g331,g330)
    c: InternalAlignment(g332,g330)
    c: Block(g330)
    c: Coincident(g333,g324)
    c: Horizontal(g333)
    c: Block(g333)
    c: Coincident(g334,g324)
    c: Coincident(g334,g250)
    c: Vertical(g334)
    c: Coincident(g335,g330)
    c: Coincident(g335,g244)
    c: Vertical(g335)
    c: Block(g336)
    c: Block(g2)
    c: Distance(g334) = 119.89
    c: Coincident(g337,g336)
    c: Coincident(g337,g2)
    c: Coincident(g338,g2)
    c: Coincident(g338,g336)
    c: Block(g3)
    c: Block(g339)
    c: Coincident(g340,g339)
    c: Coincident(g340,g3)
    c: Coincident(g341,g339)
    c: Coincident(g341,g3)
    c: Block(g341)
    c: Block(g340)
    c: Weight(g342) = 1
    c: Equal(g342,g343)
    c: Equal(g342,g344)
    c: InternalAlignment(g342,g345)
    c: InternalAlignment(g343,g345)
    c: InternalAlignment(g344,g345)
    c: InternalAlignment(g346,g345)
    c: InternalAlignment(g347,g345)
    c: Weight(g348) = 1
    c: Equal(g348,g349)
    c: Equal(g348,g350)
    c: InternalAlignment(g348,g351)
    c: InternalAlignment(g349,g351)
    c: InternalAlignment(g350,g351)
    c: InternalAlignment(g352,g351)
    c: InternalAlignment(g353,g351)
    c: Weight(g354) = 1
    c: Equal(g354,g355)
    c: Equal(g354,g356)
    c: InternalAlignment(g354,g357)
    c: InternalAlignment(g355,g357)
    c: InternalAlignment(g356,g357)
    c: InternalAlignment(g358,g357)
    c: InternalAlignment(g359,g357)
    c: Weight(g360) = 1
    c: Equal(g360,g361)
    c: Equal(g360,g362)
    c: InternalAlignment(g360,g363)
    c: InternalAlignment(g361,g363)
    c: InternalAlignment(g362,g363)
    c: InternalAlignment(g364,g363)
    c: InternalAlignment(g365,g363)
    c: Block(g363)
    c: Block(g357)
    c: Block(g351)
    c: Block(g345)
    c: Coincident(g366,g363)
    c: Coincident(g366,g345)
    c: Vertical(g366)
    c: Coincident(g367,g345)
    c: Coincident(g367,g351)
    c: Coincident(g368,g351)
    c: Coincident(g368,g357)
    c: Vertical(g368)
    c: Coincident(g369,g357)
    c: Coincident(g369,g363)
    c: Horizontal(g369)
    c: Vertical(g370)
    c: Vertical(g371)
    c: Vertical(g372)
    c: Coincident(g373,g0)
    c: Coincident(g373,g1)
    c: Horizontal(g373)
    c: Block(g373)
    c: Distance(g373) = 450
    c: Block(g371)
    c: Block(g370)
    c: Block(g372)
    c: Distance(g0) = 240
    c: Horizontal(g374)
    c: Distance(g374) = 12
    c: Coincident(g374,g370)
    c: Vertical(g375)
    c: Distance(g375) = 12
    c: Coincident(g375,g370)
    c: Coincident(g376,g374)
    c: Vertical(g376)
    c: Horizontal(g377)
    c: Vertical(g378)
    c: Distance(g378) = 6
    c: Coincident(g378,g374)
    c: Coincident(g377,g374)
    c: Block(g376)
    c: Coincident(g379,g376)
    c: Horizontal(g379)
    c: Distance(g379) = 6
    c: Vertical(g380)
    c: Distance(g380) = 3
    c: Vertical(g381)
    c: Distance(g381) = 3
    c: Coincident(g381,g370)
    c: Coincident(g375,g380)
    c: Coincident(g387,g381)
    c: Weight(g382) = 1
    c: Equal(g382,g383)
    c: Coincident(g383,g377)
    c: Equal(g382,g384)
    c: Coincident(g384,g378)
    c: Equal(g382,g385)
    c: Coincident(g385,g379)
    c: Equal(g382,g386)
    c: Coincident(g387,g380)
    c: InternalAlignment(g382-g386 -> g387) x5
    c: InternalAlignment(g388,g387)
    c: InternalAlignment(g389,g387)
    c: InternalAlignment(g390,g387)
    c: Coincident(g391,g164)
    c: Coincident(g391,g158)
    c: Horizontal(g391)
    c: Block(g387)
    c: Vertical(g392)
    c: Distance(g392) = 12
    c: Horizontal(g393)
    c: Distance(g393) = 12
    c: Coincident(g394,g393)
    c: Vertical(g394)
    c: Distance(g394) = 12
    c: Horizontal(g395)
    c: Distance(g395) = 6
    c: Coincident(g395,g393)
    c: Vertical(g396)
    c: Distance(g396) = 6
    c: Coincident(g396,g393)
    c: Vertical(g397)
    c: Distance(g397) = 3
    c: Vertical(g398)
    c: Distance(g398) = 6
    c: Coincident(g398,g397)
    c: Coincident(g404,g397)
    c: Weight(g399) = 1
    c: Equal(g399,g400)
    c: Coincident(g400,g395)
    c: Equal(g399,g401)
    c: Coincident(g401,g396)
    c: Equal(g399,g402)
    c: Equal(g399,g403)
    c: Coincident(g404,g398)
    c: InternalAlignment(g399-g403 -> g404) x5
    c: InternalAlignment(g405,g404)
    c: InternalAlignment(g406,g404)
    c: InternalAlignment(g407,g404)
    c: Coincident(g408,g392)
    c: Coincident(g408,g170)
    c: Horizontal(g408)
    c: Block(g404)
    c: Coincident(g409,g176)
    c: Coincident(g409,g392)
    c: Horizontal(g409)
    c: Block(g408)
    c: Coincident(g411,g392)
    c: PointOnObject(g411,g153)
    c: Vertical(g411)
    c: Vertical(g413)
    c: Equal(g394,g413) = 12
    c: Block(g412)
    c: Coincident(g414,g411)
FEATURE [Part::Extrusion] Extrude005
  Base = -> Sketch003
  Dir = (0,0,1)
  DirMode = 2
  FaceMakerClass = Part::FaceMakerBullseye
  LengthFwd = 24
  LengthRev = 0
  Solid = true
  Symmetric = false
